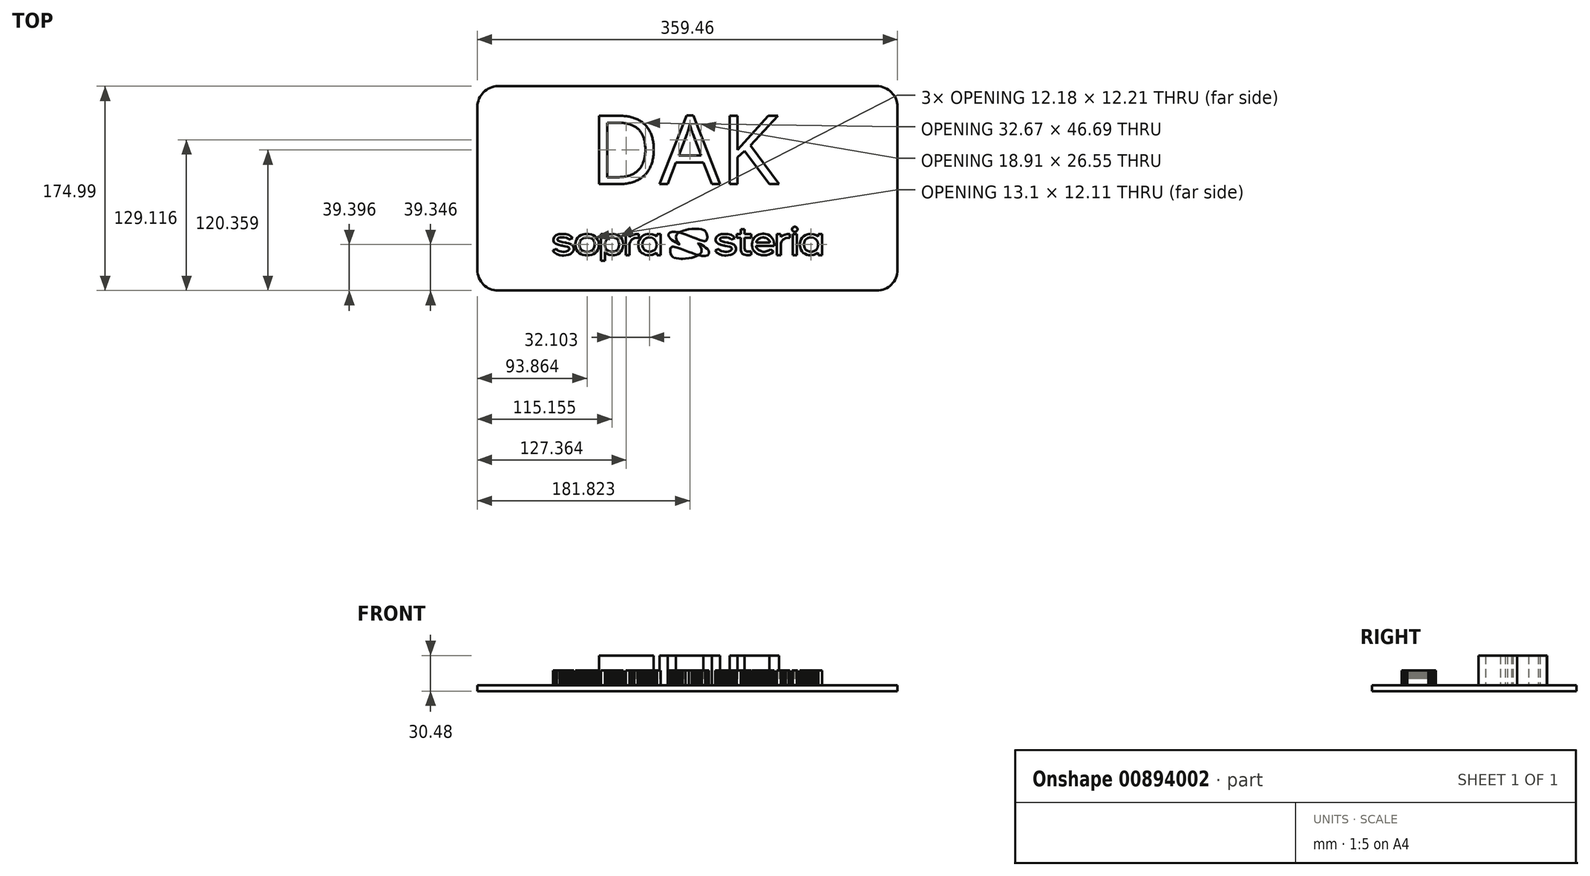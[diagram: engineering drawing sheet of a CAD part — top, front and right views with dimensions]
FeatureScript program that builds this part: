
annotation { "Feature Type Name" : "Feature", "Feature Type Description" : "" }
export const myFeature = defineFeature(function(context is Context, id is Id, definition is map)
    precondition{}
    {
        {
            var Q0;
            Q0=qCreatedBy(makeId("Top.planeOp"),FACE);
            var sketch = newSketch(context, id + "F0", { "sketchPlane" : qUnion([Q0])});
            skLineSegment(sketch, "E0", {"start": v(10.08, -9.2) * mm, "end": v(10.03, -9.23) * mm});
            skLineSegment(sketch, "E1", {"start": v(10.03, -9.23) * mm, "end": v(9.5, -9.56) * mm});
            skLineSegment(sketch, "E2", {"start": v(9.5, -9.56) * mm, "end": v(9.45, -9.6) * mm});
            skLineSegment(sketch, "E3", {"start": v(9.45, -9.6) * mm, "end": v(9.39, -9.63) * mm});
            skLineSegment(sketch, "E4", {"start": v(9.39, -9.63) * mm, "end": v(9.45, -9.64) * mm});
            skLineSegment(sketch, "E5", {"start": v(9.45, -9.64) * mm, "end": v(10.2, -9.84) * mm});
            skLineSegment(sketch, "E6", {"start": v(10.2, -9.84) * mm, "end": v(12.47, -10.24) * mm});
            skLineSegment(sketch, "E7", {"start": v(12.47, -10.24) * mm, "end": v(15.18, -10.28) * mm});
            skLineSegment(sketch, "E8", {"start": v(15.18, -10.28) * mm, "end": v(17.26, -9.63) * mm});
            skLineSegment(sketch, "E9", {"start": v(17.26, -9.63) * mm, "end": v(18.28, -8.57) * mm});
            skLineSegment(sketch, "E10", {"start": v(18.28, -8.57) * mm, "end": v(18.41, -8.16) * mm});
            skLineSegment(sketch, "E11", {"start": v(18.41, -8.16) * mm, "end": v(18.5, -7.87) * mm});
            skLineSegment(sketch, "E12", {"start": v(18.5, -7.87) * mm, "end": v(18.46, -6.9) * mm});
            skLineSegment(sketch, "E13", {"start": v(18.46, -6.9) * mm, "end": v(17.92, -5.66) * mm});
            skLineSegment(sketch, "E14", {"start": v(17.92, -5.66) * mm, "end": v(16.94, -4.44) * mm});
            skLineSegment(sketch, "E15", {"start": v(16.94, -4.44) * mm, "end": v(15.64, -3.27) * mm});
            skLineSegment(sketch, "E16", {"start": v(15.64, -3.27) * mm, "end": v(14.14, -2.18) * mm});
            skLineSegment(sketch, "E17", {"start": v(14.14, -2.18) * mm, "end": v(12.59, -1.19) * mm});
            skLineSegment(sketch, "E18", {"start": v(12.59, -1.19) * mm, "end": v(11.1, -0.32) * mm});
            skLineSegment(sketch, "E19", {"start": v(11.1, -0.32) * mm, "end": v(10.12, 0.22) * mm});
            skLineSegment(sketch, "E20", {"start": v(10.12, 0.22) * mm, "end": v(9.8, 0.4) * mm});
            skLineSegment(sketch, "E21", {"start": v(9.8, 0.4) * mm, "end": v(9.7, 0.45) * mm});
            skLineSegment(sketch, "E22", {"start": v(9.7, 0.45) * mm, "end": v(9.38, 0.56) * mm});
            skLineSegment(sketch, "E23", {"start": v(9.38, 0.56) * mm, "end": v(9.13, 0.54) * mm});
            skLineSegment(sketch, "E24", {"start": v(9.13, 0.54) * mm, "end": v(9.08, 0.36) * mm});
            skLineSegment(sketch, "E25", {"start": v(9.08, 0.36) * mm, "end": v(9.2, 0.12) * mm});
            skLineSegment(sketch, "E26", {"start": v(9.2, 0.12) * mm, "end": v(9.27, 0.05) * mm});
            skLineSegment(sketch, "E27", {"start": v(9.27, 0.05) * mm, "end": v(9.47, -0.18) * mm});
            skLineSegment(sketch, "E28", {"start": v(9.47, -0.18) * mm, "end": v(10.02, -0.89) * mm});
            skLineSegment(sketch, "E29", {"start": v(10.02, -0.89) * mm, "end": v(10.77, -1.98) * mm});
            skLineSegment(sketch, "E30", {"start": v(10.77, -1.98) * mm, "end": v(11.41, -3.18) * mm});
            skLineSegment(sketch, "E31", {"start": v(11.41, -3.18) * mm, "end": v(11.87, -4.45) * mm});
            skLineSegment(sketch, "E32", {"start": v(11.87, -4.45) * mm, "end": v(12.06, -5.73) * mm});
            skLineSegment(sketch, "E33", {"start": v(12.06, -5.73) * mm, "end": v(11.88, -6.98) * mm});
            skLineSegment(sketch, "E34", {"start": v(11.88, -6.98) * mm, "end": v(11.25, -8.15) * mm});
            skLineSegment(sketch, "E35", {"start": v(11.25, -8.15) * mm, "end": v(10.4, -8.99) * mm});
            skLineSegment(sketch, "E36", {"start": v(10.4, -8.99) * mm, "end": v(10.08, -9.2) * mm});
            skLineSegment(sketch, "E37", {"start": v(45.51, 5.32) * mm, "end": v(42.05, 5.32) * mm});
            skLineSegment(sketch, "E38", {"start": v(42.05, 5.32) * mm, "end": v(42.05, 8.22) * mm});
            skLineSegment(sketch, "E39", {"start": v(42.05, 8.22) * mm, "end": v(45.51, 8.22) * mm});
            skLineSegment(sketch, "E40", {"start": v(45.51, 8.22) * mm, "end": v(45.51, 12.52) * mm});
            skLineSegment(sketch, "E41", {"start": v(45.51, 12.52) * mm, "end": v(48.87, 12.52) * mm});
            skLineSegment(sketch, "E42", {"start": v(48.87, 12.52) * mm, "end": v(48.87, 8.22) * mm});
            skLineSegment(sketch, "E43", {"start": v(48.87, 8.22) * mm, "end": v(54.4, 8.22) * mm});
            skLineSegment(sketch, "E44", {"start": v(54.4, 8.22) * mm, "end": v(54.4, 5.32) * mm});
            skLineSegment(sketch, "E45", {"start": v(54.4, 5.32) * mm, "end": v(48.87, 5.32) * mm});
            skLineSegment(sketch, "E46", {"start": v(48.87, 5.32) * mm, "end": v(48.87, -3.42) * mm});
            skLineSegment(sketch, "E47", {"start": v(48.87, -3.42) * mm, "end": v(48.87, -3.78) * mm});
            skLineSegment(sketch, "E48", {"start": v(48.87, -3.78) * mm, "end": v(49, -4.86) * mm});
            skLineSegment(sketch, "E49", {"start": v(49, -4.86) * mm, "end": v(49.52, -5.9) * mm});
            skLineSegment(sketch, "E50", {"start": v(49.52, -5.9) * mm, "end": v(50.56, -6.53) * mm});
            skLineSegment(sketch, "E51", {"start": v(50.56, -6.53) * mm, "end": v(51.85, -6.74) * mm});
            skLineSegment(sketch, "E52", {"start": v(51.85, -6.74) * mm, "end": v(52.28, -6.74) * mm});
            skLineSegment(sketch, "E53", {"start": v(52.28, -6.74) * mm, "end": v(52.48, -6.74) * mm});
            skLineSegment(sketch, "E54", {"start": v(52.48, -6.74) * mm, "end": v(53.08, -6.7) * mm});
            skLineSegment(sketch, "E55", {"start": v(53.08, -6.7) * mm, "end": v(53.81, -6.6) * mm});
            skLineSegment(sketch, "E56", {"start": v(53.81, -6.6) * mm, "end": v(54.34, -6.49) * mm});
            skLineSegment(sketch, "E57", {"start": v(54.34, -6.49) * mm, "end": v(54.55, -6.44) * mm});
            skLineSegment(sketch, "E58", {"start": v(54.55, -6.44) * mm, "end": v(54.55, -9.46) * mm});
            skLineSegment(sketch, "E59", {"start": v(54.55, -9.46) * mm, "end": v(54.26, -9.5) * mm});
            skLineSegment(sketch, "E60", {"start": v(54.26, -9.5) * mm, "end": v(52.94, -9.65) * mm});
            skLineSegment(sketch, "E61", {"start": v(52.94, -9.65) * mm, "end": v(51.64, -9.71) * mm});
            skLineSegment(sketch, "E62", {"start": v(51.64, -9.71) * mm, "end": v(51.21, -9.71) * mm});
            skLineSegment(sketch, "E63", {"start": v(51.21, -9.71) * mm, "end": v(50.77, -9.71) * mm});
            skLineSegment(sketch, "E64", {"start": v(50.77, -9.71) * mm, "end": v(49.45, -9.54) * mm});
            skLineSegment(sketch, "E65", {"start": v(49.45, -9.54) * mm, "end": v(48.09, -9.08) * mm});
            skLineSegment(sketch, "E66", {"start": v(48.09, -9.08) * mm, "end": v(47.08, -8.4) * mm});
            skLineSegment(sketch, "E67", {"start": v(47.08, -8.4) * mm, "end": v(46.38, -7.54) * mm});
            skLineSegment(sketch, "E68", {"start": v(46.38, -7.54) * mm, "end": v(45.92, -6.6) * mm});
            skLineSegment(sketch, "E69", {"start": v(45.92, -6.6) * mm, "end": v(45.66, -5.61) * mm});
            skLineSegment(sketch, "E70", {"start": v(45.66, -5.61) * mm, "end": v(45.54, -4.66) * mm});
            skLineSegment(sketch, "E71", {"start": v(45.54, -4.66) * mm, "end": v(45.51, -4.02) * mm});
            skLineSegment(sketch, "E72", {"start": v(45.51, -4.02) * mm, "end": v(45.51, -3.81) * mm});
            skLineSegment(sketch, "E73", {"start": v(45.51, -3.81) * mm, "end": v(45.51, 5.32) * mm});
            skLineSegment(sketch, "E74", {"start": v(93.55, -9.75) * mm, "end": v(90.11, -9.75) * mm});
            skLineSegment(sketch, "E75", {"start": v(90.11, -9.75) * mm, "end": v(90.11, 8.23) * mm});
            skLineSegment(sketch, "E76", {"start": v(90.11, 8.23) * mm, "end": v(93.55, 8.23) * mm});
            skLineSegment(sketch, "E77", {"start": v(93.55, 8.23) * mm, "end": v(93.55, -9.75) * mm});
            skLineSegment(sketch, "E78", {"start": v(96.13, -0.6) * mm, "end": v(96.13, 0) * mm});
            skLineSegment(sketch, "E79", {"start": v(96.13, 0) * mm, "end": v(96.37, 1.74) * mm});
            skLineSegment(sketch, "E80", {"start": v(96.37, 1.74) * mm, "end": v(97.04, 3.68) * mm});
            skLineSegment(sketch, "E81", {"start": v(97.04, 3.68) * mm, "end": v(98.06, 5.25) * mm});
            skLineSegment(sketch, "E82", {"start": v(98.06, 5.25) * mm, "end": v(99.34, 6.48) * mm});
            skLineSegment(sketch, "E83", {"start": v(99.34, 6.48) * mm, "end": v(100.8, 7.39) * mm});
            skLineSegment(sketch, "E84", {"start": v(100.8, 7.39) * mm, "end": v(102.34, 8) * mm});
            skLineSegment(sketch, "E85", {"start": v(102.34, 8) * mm, "end": v(103.9, 8.36) * mm});
            skLineSegment(sketch, "E86", {"start": v(103.9, 8.36) * mm, "end": v(105.02, 8.47) * mm});
            skLineSegment(sketch, "E87", {"start": v(105.02, 8.47) * mm, "end": v(105.4, 8.47) * mm});
            skLineSegment(sketch, "E88", {"start": v(105.4, 8.47) * mm, "end": v(106.1, 8.47) * mm});
            skLineSegment(sketch, "E89", {"start": v(106.1, 8.47) * mm, "end": v(108.22, 8.08) * mm});
            skLineSegment(sketch, "E90", {"start": v(108.22, 8.08) * mm, "end": v(110.22, 7.23) * mm});
            skLineSegment(sketch, "E91", {"start": v(110.22, 7.23) * mm, "end": v(111.4, 6.38) * mm});
            skLineSegment(sketch, "E92", {"start": v(111.4, 6.38) * mm, "end": v(111.8, 6) * mm});
            skLineSegment(sketch, "E93", {"start": v(111.8, 6) * mm, "end": v(111.98, 8.23) * mm});
            skLineSegment(sketch, "E94", {"start": v(111.98, 8.23) * mm, "end": v(115.12, 8.23) * mm});
            skLineSegment(sketch, "E95", {"start": v(115.12, 8.23) * mm, "end": v(115.12, -9.8) * mm});
            skLineSegment(sketch, "E96", {"start": v(115.12, -9.8) * mm, "end": v(111.98, -9.8) * mm});
            skLineSegment(sketch, "E97", {"start": v(111.98, -9.8) * mm, "end": v(111.8, -7.4) * mm});
            skLineSegment(sketch, "E98", {"start": v(111.8, -7.4) * mm, "end": v(111.4, -7.78) * mm});
            skLineSegment(sketch, "E99", {"start": v(111.4, -7.78) * mm, "end": v(110.19, -8.6) * mm});
            skLineSegment(sketch, "E100", {"start": v(110.19, -8.6) * mm, "end": v(108.17, -9.42) * mm});
            skLineSegment(sketch, "E101", {"start": v(108.17, -9.42) * mm, "end": v(106.06, -9.8) * mm});
            skLineSegment(sketch, "E102", {"start": v(106.06, -9.8) * mm, "end": v(105.36, -9.8) * mm});
            skLineSegment(sketch, "E103", {"start": v(105.36, -9.8) * mm, "end": v(104.95, -9.8) * mm});
            skLineSegment(sketch, "E104", {"start": v(104.95, -9.8) * mm, "end": v(103.72, -9.67) * mm});
            skLineSegment(sketch, "E105", {"start": v(103.72, -9.67) * mm, "end": v(102.1, -9.3) * mm});
            skLineSegment(sketch, "E106", {"start": v(102.1, -9.3) * mm, "end": v(100.54, -8.65) * mm});
            skLineSegment(sketch, "E107", {"start": v(100.54, -8.65) * mm, "end": v(99.13, -7.7) * mm});
            skLineSegment(sketch, "E108", {"start": v(99.13, -7.7) * mm, "end": v(97.91, -6.45) * mm});
            skLineSegment(sketch, "E109", {"start": v(97.91, -6.45) * mm, "end": v(96.96, -4.86) * mm});
            skLineSegment(sketch, "E110", {"start": v(96.96, -4.86) * mm, "end": v(96.35, -2.9) * mm});
            skLineSegment(sketch, "E111", {"start": v(96.35, -2.9) * mm, "end": v(96.13, -1.17) * mm});
            skLineSegment(sketch, "E112", {"start": v(96.13, -1.17) * mm, "end": v(96.13, -0.6) * mm});
            skLineSegment(sketch, "E113", {"start": v(99.62, -0.63) * mm, "end": v(99.62, -1.04) * mm});
            skLineSegment(sketch, "E114", {"start": v(99.62, -1.04) * mm, "end": v(99.8, -2.3) * mm});
            skLineSegment(sketch, "E115", {"start": v(99.8, -2.3) * mm, "end": v(100.28, -3.65) * mm});
            skLineSegment(sketch, "E116", {"start": v(100.28, -3.65) * mm, "end": v(101, -4.72) * mm});
            skLineSegment(sketch, "E117", {"start": v(101, -4.72) * mm, "end": v(101.88, -5.53) * mm});
            skLineSegment(sketch, "E118", {"start": v(101.88, -5.53) * mm, "end": v(102.85, -6.1) * mm});
            skLineSegment(sketch, "E119", {"start": v(102.85, -6.1) * mm, "end": v(103.84, -6.48) * mm});
            skLineSegment(sketch, "E120", {"start": v(103.84, -6.48) * mm, "end": v(104.77, -6.69) * mm});
            skLineSegment(sketch, "E121", {"start": v(104.77, -6.69) * mm, "end": v(105.37, -6.75) * mm});
            skLineSegment(sketch, "E122", {"start": v(105.37, -6.75) * mm, "end": v(105.58, -6.75) * mm});
            skLineSegment(sketch, "E123", {"start": v(105.58, -6.75) * mm, "end": v(106.2, -6.75) * mm});
            skLineSegment(sketch, "E124", {"start": v(106.2, -6.75) * mm, "end": v(108.09, -6.36) * mm});
            skLineSegment(sketch, "E125", {"start": v(108.09, -6.36) * mm, "end": v(110.06, -5.2) * mm});
            skLineSegment(sketch, "E126", {"start": v(110.06, -5.2) * mm, "end": v(111.34, -3.27) * mm});
            skLineSegment(sketch, "E127", {"start": v(111.34, -3.27) * mm, "end": v(111.8, -1.23) * mm});
            skLineSegment(sketch, "E128", {"start": v(111.8, -1.23) * mm, "end": v(111.8, -0.56) * mm});
            skLineSegment(sketch, "E129", {"start": v(111.8, -0.56) * mm, "end": v(111.8, 0.11) * mm});
            skLineSegment(sketch, "E130", {"start": v(111.8, 0.11) * mm, "end": v(111.3, 2.13) * mm});
            skLineSegment(sketch, "E131", {"start": v(111.3, 2.13) * mm, "end": v(109.92, 4) * mm});
            skLineSegment(sketch, "E132", {"start": v(109.92, 4) * mm, "end": v(107.92, 5.1) * mm});
            skLineSegment(sketch, "E133", {"start": v(107.92, 5.1) * mm, "end": v(106.13, 5.46) * mm});
            skLineSegment(sketch, "E134", {"start": v(106.13, 5.46) * mm, "end": v(105.54, 5.46) * mm});
            skLineSegment(sketch, "E135", {"start": v(105.54, 5.46) * mm, "end": v(105.34, 5.46) * mm});
            skLineSegment(sketch, "E136", {"start": v(105.34, 5.46) * mm, "end": v(104.74, 5.4) * mm});
            skLineSegment(sketch, "E137", {"start": v(104.74, 5.4) * mm, "end": v(103.82, 5.21) * mm});
            skLineSegment(sketch, "E138", {"start": v(103.82, 5.21) * mm, "end": v(102.84, 4.85) * mm});
            skLineSegment(sketch, "E139", {"start": v(102.84, 4.85) * mm, "end": v(101.87, 4.28) * mm});
            skLineSegment(sketch, "E140", {"start": v(101.87, 4.28) * mm, "end": v(101, 3.49) * mm});
            skLineSegment(sketch, "E141", {"start": v(101, 3.49) * mm, "end": v(100.28, 2.42) * mm});
            skLineSegment(sketch, "E142", {"start": v(100.28, 2.42) * mm, "end": v(99.8, 1.06) * mm});
            skLineSegment(sketch, "E143", {"start": v(99.8, 1.06) * mm, "end": v(99.62, -0.2) * mm});
            skLineSegment(sketch, "E144", {"start": v(99.62, -0.2) * mm, "end": v(99.62, -0.63) * mm});
            skLineSegment(sketch, "E145", {"start": v(94.08, 12.39) * mm, "end": v(94.08, 12.6) * mm});
            skLineSegment(sketch, "E146", {"start": v(94.08, 12.6) * mm, "end": v(93.9, 13.26) * mm});
            skLineSegment(sketch, "E147", {"start": v(93.9, 13.26) * mm, "end": v(93.42, 13.98) * mm});
            skLineSegment(sketch, "E148", {"start": v(93.42, 13.98) * mm, "end": v(92.7, 14.46) * mm});
            skLineSegment(sketch, "E149", {"start": v(92.7, 14.46) * mm, "end": v(92.05, 14.64) * mm});
            skLineSegment(sketch, "E150", {"start": v(92.05, 14.64) * mm, "end": v(91.83, 14.64) * mm});
            skLineSegment(sketch, "E151", {"start": v(91.83, 14.64) * mm, "end": v(91.61, 14.64) * mm});
            skLineSegment(sketch, "E152", {"start": v(91.61, 14.64) * mm, "end": v(90.96, 14.46) * mm});
            skLineSegment(sketch, "E153", {"start": v(90.96, 14.46) * mm, "end": v(90.24, 13.98) * mm});
            skLineSegment(sketch, "E154", {"start": v(90.24, 13.98) * mm, "end": v(89.76, 13.26) * mm});
            skLineSegment(sketch, "E155", {"start": v(89.76, 13.26) * mm, "end": v(89.58, 12.6) * mm});
            skLineSegment(sketch, "E156", {"start": v(89.58, 12.6) * mm, "end": v(89.58, 12.39) * mm});
            skLineSegment(sketch, "E157", {"start": v(89.58, 12.39) * mm, "end": v(89.58, 12.17) * mm});
            skLineSegment(sketch, "E158", {"start": v(89.58, 12.17) * mm, "end": v(89.76, 11.51) * mm});
            skLineSegment(sketch, "E159", {"start": v(89.76, 11.51) * mm, "end": v(90.24, 10.8) * mm});
            skLineSegment(sketch, "E160", {"start": v(90.24, 10.8) * mm, "end": v(90.96, 10.32) * mm});
            skLineSegment(sketch, "E161", {"start": v(90.96, 10.32) * mm, "end": v(91.61, 10.14) * mm});
            skLineSegment(sketch, "E162", {"start": v(91.61, 10.14) * mm, "end": v(91.83, 10.14) * mm});
            skLineSegment(sketch, "E163", {"start": v(91.83, 10.14) * mm, "end": v(92.05, 10.14) * mm});
            skLineSegment(sketch, "E164", {"start": v(92.05, 10.14) * mm, "end": v(92.7, 10.32) * mm});
            skLineSegment(sketch, "E165", {"start": v(92.7, 10.32) * mm, "end": v(93.42, 10.8) * mm});
            skLineSegment(sketch, "E166", {"start": v(93.42, 10.8) * mm, "end": v(93.9, 11.51) * mm});
            skLineSegment(sketch, "E167", {"start": v(93.9, 11.51) * mm, "end": v(94.08, 12.17) * mm});
            skLineSegment(sketch, "E168", {"start": v(94.08, 12.17) * mm, "end": v(94.08, 12.39) * mm});
            skLineSegment(sketch, "E169", {"start": v(87.6, 5.14) * mm, "end": v(87.6, 8.19) * mm});
            skLineSegment(sketch, "E170", {"start": v(87.6, 8.19) * mm, "end": v(87.01, 8.24) * mm});
            skLineSegment(sketch, "E171", {"start": v(87.01, 8.24) * mm, "end": v(85.24, 8.2) * mm});
            skLineSegment(sketch, "E172", {"start": v(85.24, 8.2) * mm, "end": v(83.2, 7.81) * mm});
            skLineSegment(sketch, "E173", {"start": v(83.2, 7.81) * mm, "end": v(81.46, 6.99) * mm});
            skLineSegment(sketch, "E174", {"start": v(81.46, 6.99) * mm, "end": v(80.3, 6.1) * mm});
            skLineSegment(sketch, "E175", {"start": v(80.3, 6.1) * mm, "end": v(79.96, 5.74) * mm});
            skLineSegment(sketch, "E176", {"start": v(79.96, 5.74) * mm, "end": v(79.79, 8.23) * mm});
            skLineSegment(sketch, "E177", {"start": v(79.79, 8.23) * mm, "end": v(76.52, 8.23) * mm});
            skLineSegment(sketch, "E178", {"start": v(76.52, 8.23) * mm, "end": v(76.52, -9.78) * mm});
            skLineSegment(sketch, "E179", {"start": v(76.52, -9.78) * mm, "end": v(79.96, -9.78) * mm});
            skLineSegment(sketch, "E180", {"start": v(79.96, -9.78) * mm, "end": v(79.96, -0.45) * mm});
            skLineSegment(sketch, "E181", {"start": v(79.96, -0.45) * mm, "end": v(79.96, 0.05) * mm});
            skLineSegment(sketch, "E182", {"start": v(79.96, 0.05) * mm, "end": v(80.38, 1.57) * mm});
            skLineSegment(sketch, "E183", {"start": v(80.38, 1.57) * mm, "end": v(81.7, 3.44) * mm});
            skLineSegment(sketch, "E184", {"start": v(81.7, 3.44) * mm, "end": v(84.07, 4.76) * mm});
            skLineSegment(sketch, "E185", {"start": v(84.07, 4.76) * mm, "end": v(86.72, 5.2) * mm});
            skLineSegment(sketch, "E186", {"start": v(86.72, 5.2) * mm, "end": v(87.6, 5.14) * mm});
            skLineSegment(sketch, "E187", {"start": v(70.47, 0.88) * mm, "end": v(70.47, 1.1) * mm});
            skLineSegment(sketch, "E188", {"start": v(70.47, 1.1) * mm, "end": v(70.35, 1.78) * mm});
            skLineSegment(sketch, "E189", {"start": v(70.35, 1.78) * mm, "end": v(70.03, 2.62) * mm});
            skLineSegment(sketch, "E190", {"start": v(70.03, 2.62) * mm, "end": v(69.53, 3.38) * mm});
            skLineSegment(sketch, "E191", {"start": v(69.53, 3.38) * mm, "end": v(68.86, 4.04) * mm});
            skLineSegment(sketch, "E192", {"start": v(68.86, 4.04) * mm, "end": v(68.04, 4.6) * mm});
            skLineSegment(sketch, "E193", {"start": v(68.04, 4.6) * mm, "end": v(67.11, 5.01) * mm});
            skLineSegment(sketch, "E194", {"start": v(67.11, 5.01) * mm, "end": v(66.08, 5.28) * mm});
            skLineSegment(sketch, "E195", {"start": v(66.08, 5.28) * mm, "end": v(65.26, 5.37) * mm});
            skLineSegment(sketch, "E196", {"start": v(65.26, 5.37) * mm, "end": v(64.98, 5.37) * mm});
            skLineSegment(sketch, "E197", {"start": v(64.98, 5.37) * mm, "end": v(64.4, 5.37) * mm});
            skLineSegment(sketch, "E198", {"start": v(64.4, 5.37) * mm, "end": v(62.69, 5.02) * mm});
            skLineSegment(sketch, "E199", {"start": v(62.69, 5.02) * mm, "end": v(60.78, 4.06) * mm});
            skLineSegment(sketch, "E200", {"start": v(60.78, 4.06) * mm, "end": v(59.44, 2.63) * mm});
            skLineSegment(sketch, "E201", {"start": v(59.44, 2.63) * mm, "end": v(58.89, 1.33) * mm});
            skLineSegment(sketch, "E202", {"start": v(58.89, 1.33) * mm, "end": v(58.85, 0.88) * mm});
            skLineSegment(sketch, "E203", {"start": v(58.85, 0.88) * mm, "end": v(70.47, 0.88) * mm});
            skLineSegment(sketch, "E204", {"start": v(55.22, -0.66) * mm, "end": v(55.22, -0.16) * mm});
            skLineSegment(sketch, "E205", {"start": v(55.22, -0.16) * mm, "end": v(55.4, 1.35) * mm});
            skLineSegment(sketch, "E206", {"start": v(55.4, 1.35) * mm, "end": v(55.95, 3.16) * mm});
            skLineSegment(sketch, "E207", {"start": v(55.95, 3.16) * mm, "end": v(56.83, 4.74) * mm});
            skLineSegment(sketch, "E208", {"start": v(56.83, 4.74) * mm, "end": v(58, 6.07) * mm});
            skLineSegment(sketch, "E209", {"start": v(58, 6.07) * mm, "end": v(59.42, 7.14) * mm});
            skLineSegment(sketch, "E210", {"start": v(59.42, 7.14) * mm, "end": v(61.07, 7.93) * mm});
            skLineSegment(sketch, "E211", {"start": v(61.07, 7.93) * mm, "end": v(62.92, 8.42) * mm});
            skLineSegment(sketch, "E212", {"start": v(62.92, 8.42) * mm, "end": v(64.43, 8.58) * mm});
            skLineSegment(sketch, "E213", {"start": v(64.43, 8.58) * mm, "end": v(64.93, 8.58) * mm});
            skLineSegment(sketch, "E214", {"start": v(64.93, 8.58) * mm, "end": v(65.43, 8.58) * mm});
            skLineSegment(sketch, "E215", {"start": v(65.43, 8.58) * mm, "end": v(66.92, 8.4) * mm});
            skLineSegment(sketch, "E216", {"start": v(66.92, 8.4) * mm, "end": v(68.71, 7.87) * mm});
            skLineSegment(sketch, "E217", {"start": v(68.71, 7.87) * mm, "end": v(70.3, 7.05) * mm});
            skLineSegment(sketch, "E218", {"start": v(70.3, 7.05) * mm, "end": v(71.66, 5.95) * mm});
            skLineSegment(sketch, "E219", {"start": v(71.66, 5.95) * mm, "end": v(72.75, 4.63) * mm});
            skLineSegment(sketch, "E220", {"start": v(72.75, 4.63) * mm, "end": v(73.56, 3.11) * mm});
            skLineSegment(sketch, "E221", {"start": v(73.56, 3.11) * mm, "end": v(74.07, 1.44) * mm});
            skLineSegment(sketch, "E222", {"start": v(74.07, 1.44) * mm, "end": v(74.24, 0.1) * mm});
            skLineSegment(sketch, "E223", {"start": v(74.24, 0.1) * mm, "end": v(74.24, -0.35) * mm});
            skLineSegment(sketch, "E224", {"start": v(74.24, -0.35) * mm, "end": v(74.23, -0.82) * mm});
            skLineSegment(sketch, "E225", {"start": v(74.23, -0.82) * mm, "end": v(74.19, -1.64) * mm});
            skLineSegment(sketch, "E226", {"start": v(74.19, -1.64) * mm, "end": v(74.17, -1.8) * mm});
            skLineSegment(sketch, "E227", {"start": v(74.17, -1.8) * mm, "end": v(58.8, -1.87) * mm});
            skLineSegment(sketch, "E228", {"start": v(58.8, -1.87) * mm, "end": v(58.82, -2.36) * mm});
            skLineSegment(sketch, "E229", {"start": v(58.82, -2.36) * mm, "end": v(59.43, -3.8) * mm});
            skLineSegment(sketch, "E230", {"start": v(59.43, -3.8) * mm, "end": v(60.94, -5.35) * mm});
            skLineSegment(sketch, "E231", {"start": v(60.94, -5.35) * mm, "end": v(63.04, -6.38) * mm});
            skLineSegment(sketch, "E232", {"start": v(63.04, -6.38) * mm, "end": v(64.86, -6.75) * mm});
            skLineSegment(sketch, "E233", {"start": v(64.86, -6.75) * mm, "end": v(65.46, -6.75) * mm});
            skLineSegment(sketch, "E234", {"start": v(65.46, -6.75) * mm, "end": v(66.06, -6.75) * mm});
            skLineSegment(sketch, "E235", {"start": v(66.06, -6.75) * mm, "end": v(67.85, -6.4) * mm});
            skLineSegment(sketch, "E236", {"start": v(67.85, -6.4) * mm, "end": v(69.64, -5.64) * mm});
            skLineSegment(sketch, "E237", {"start": v(69.64, -5.64) * mm, "end": v(70.75, -4.89) * mm});
            skLineSegment(sketch, "E238", {"start": v(70.75, -4.89) * mm, "end": v(71.14, -4.54) * mm});
            skLineSegment(sketch, "E239", {"start": v(71.14, -4.54) * mm, "end": v(73.6, -6.7) * mm});
            skLineSegment(sketch, "E240", {"start": v(73.6, -6.7) * mm, "end": v(73.16, -7.12) * mm});
            skLineSegment(sketch, "E241", {"start": v(73.16, -7.12) * mm, "end": v(71.68, -8.2) * mm});
            skLineSegment(sketch, "E242", {"start": v(71.68, -8.2) * mm, "end": v(69.69, -9.17) * mm});
            skLineSegment(sketch, "E243", {"start": v(69.69, -9.17) * mm, "end": v(67.61, -9.68) * mm});
            skLineSegment(sketch, "E244", {"start": v(67.61, -9.68) * mm, "end": v(66, -9.83) * mm});
            skLineSegment(sketch, "E245", {"start": v(66, -9.83) * mm, "end": v(65.46, -9.83) * mm});
            skLineSegment(sketch, "E246", {"start": v(65.46, -9.83) * mm, "end": v(64.92, -9.83) * mm});
            skLineSegment(sketch, "E247", {"start": v(64.92, -9.83) * mm, "end": v(63.28, -9.67) * mm});
            skLineSegment(sketch, "E248", {"start": v(63.28, -9.67) * mm, "end": v(61.3, -9.2) * mm});
            skLineSegment(sketch, "E249", {"start": v(61.3, -9.2) * mm, "end": v(59.56, -8.42) * mm});
            skLineSegment(sketch, "E250", {"start": v(59.56, -8.42) * mm, "end": v(58.07, -7.37) * mm});
            skLineSegment(sketch, "E251", {"start": v(58.07, -7.37) * mm, "end": v(56.86, -6.07) * mm});
            skLineSegment(sketch, "E252", {"start": v(56.86, -6.07) * mm, "end": v(55.97, -4.52) * mm});
            skLineSegment(sketch, "E253", {"start": v(55.97, -4.52) * mm, "end": v(55.4, -2.76) * mm});
            skLineSegment(sketch, "E254", {"start": v(55.4, -2.76) * mm, "end": v(55.22, -1.3) * mm});
            skLineSegment(sketch, "E255", {"start": v(55.22, -1.3) * mm, "end": v(55.22, -0.8) * mm});
            skLineSegment(sketch, "E256", {"start": v(55.22, -0.8) * mm, "end": v(55.22, -0.66) * mm});
            skLineSegment(sketch, "E257", {"start": v(34.69, 0.96) * mm, "end": v(34.05, 1.07) * mm});
            skLineSegment(sketch, "E258", {"start": v(34.05, 1.07) * mm, "end": v(32.15, 1.41) * mm});
            skLineSegment(sketch, "E259", {"start": v(32.15, 1.41) * mm, "end": v(29.96, 1.92) * mm});
            skLineSegment(sketch, "E260", {"start": v(29.96, 1.92) * mm, "end": v(28.4, 2.61) * mm});
            skLineSegment(sketch, "E261", {"start": v(28.4, 2.61) * mm, "end": v(27.82, 3.37) * mm});
            skLineSegment(sketch, "E262", {"start": v(27.82, 3.37) * mm, "end": v(27.82, 3.62) * mm});
            skLineSegment(sketch, "E263", {"start": v(27.82, 3.62) * mm, "end": v(27.82, 3.81) * mm});
            skLineSegment(sketch, "E264", {"start": v(27.82, 3.81) * mm, "end": v(28.03, 4.38) * mm});
            skLineSegment(sketch, "E265", {"start": v(28.03, 4.38) * mm, "end": v(28.72, 5) * mm});
            skLineSegment(sketch, "E266", {"start": v(28.72, 5) * mm, "end": v(29.98, 5.44) * mm});
            skLineSegment(sketch, "E267", {"start": v(29.98, 5.44) * mm, "end": v(31.42, 5.6) * mm});
            skLineSegment(sketch, "E268", {"start": v(31.42, 5.6) * mm, "end": v(31.9, 5.6) * mm});
            skLineSegment(sketch, "E269", {"start": v(31.9, 5.6) * mm, "end": v(32.32, 5.6) * mm});
            skLineSegment(sketch, "E270", {"start": v(32.32, 5.6) * mm, "end": v(33.61, 5.5) * mm});
            skLineSegment(sketch, "E271", {"start": v(33.61, 5.5) * mm, "end": v(35.25, 5.14) * mm});
            skLineSegment(sketch, "E272", {"start": v(35.25, 5.14) * mm, "end": v(36.6, 4.49) * mm});
            skLineSegment(sketch, "E273", {"start": v(36.6, 4.49) * mm, "end": v(37.32, 3.77) * mm});
            skLineSegment(sketch, "E274", {"start": v(37.32, 3.77) * mm, "end": v(37.45, 3.48) * mm});
            skLineSegment(sketch, "E275", {"start": v(37.45, 3.48) * mm, "end": v(40.64, 4.83) * mm});
            skLineSegment(sketch, "E276", {"start": v(40.64, 4.83) * mm, "end": v(40.41, 5.28) * mm});
            skLineSegment(sketch, "E277", {"start": v(40.41, 5.28) * mm, "end": v(39.3, 6.43) * mm});
            skLineSegment(sketch, "E278", {"start": v(39.3, 6.43) * mm, "end": v(37.25, 7.56) * mm});
            skLineSegment(sketch, "E279", {"start": v(37.25, 7.56) * mm, "end": v(34.64, 8.24) * mm});
            skLineSegment(sketch, "E280", {"start": v(34.64, 8.24) * mm, "end": v(32.4, 8.46) * mm});
            skLineSegment(sketch, "E281", {"start": v(32.4, 8.46) * mm, "end": v(31.66, 8.46) * mm});
            skLineSegment(sketch, "E282", {"start": v(31.66, 8.46) * mm, "end": v(30.98, 8.46) * mm});
            skLineSegment(sketch, "E283", {"start": v(30.98, 8.46) * mm, "end": v(28.95, 8.19) * mm});
            skLineSegment(sketch, "E284", {"start": v(28.95, 8.19) * mm, "end": v(26.53, 7.31) * mm});
            skLineSegment(sketch, "E285", {"start": v(26.53, 7.31) * mm, "end": v(24.8, 5.75) * mm});
            skLineSegment(sketch, "E286", {"start": v(24.8, 5.75) * mm, "end": v(24.13, 4) * mm});
            skLineSegment(sketch, "E287", {"start": v(24.13, 4) * mm, "end": v(24.13, 3.41) * mm});
            skLineSegment(sketch, "E288", {"start": v(24.13, 3.41) * mm, "end": v(24.13, 2.9) * mm});
            skLineSegment(sketch, "E289", {"start": v(24.13, 2.9) * mm, "end": v(24.66, 1.4) * mm});
            skLineSegment(sketch, "E290", {"start": v(24.66, 1.4) * mm, "end": v(26.18, 0.02) * mm});
            skLineSegment(sketch, "E291", {"start": v(26.18, 0.02) * mm, "end": v(28.59, -0.93) * mm});
            skLineSegment(sketch, "E292", {"start": v(28.59, -0.93) * mm, "end": v(31, -1.5) * mm});
            skLineSegment(sketch, "E293", {"start": v(31, -1.5) * mm, "end": v(31.8, -1.66) * mm});
            skLineSegment(sketch, "E294", {"start": v(31.8, -1.66) * mm, "end": v(32.38, -1.77) * mm});
            skLineSegment(sketch, "E295", {"start": v(32.38, -1.77) * mm, "end": v(34.1, -2.08) * mm});
            skLineSegment(sketch, "E296", {"start": v(34.1, -2.08) * mm, "end": v(36.07, -2.55) * mm});
            skLineSegment(sketch, "E297", {"start": v(36.07, -2.55) * mm, "end": v(37.43, -3.23) * mm});
            skLineSegment(sketch, "E298", {"start": v(37.43, -3.23) * mm, "end": v(37.94, -4.02) * mm});
            skLineSegment(sketch, "E299", {"start": v(37.94, -4.02) * mm, "end": v(37.94, -4.28) * mm});
            skLineSegment(sketch, "E300", {"start": v(37.94, -4.28) * mm, "end": v(37.94, -4.5) * mm});
            skLineSegment(sketch, "E301", {"start": v(37.94, -4.5) * mm, "end": v(37.65, -5.13) * mm});
            skLineSegment(sketch, "E302", {"start": v(37.65, -5.13) * mm, "end": v(36.76, -5.93) * mm});
            skLineSegment(sketch, "E303", {"start": v(36.76, -5.93) * mm, "end": v(35.19, -6.52) * mm});
            skLineSegment(sketch, "E304", {"start": v(35.19, -6.52) * mm, "end": v(33.45, -6.76) * mm});
            skLineSegment(sketch, "E305", {"start": v(33.45, -6.76) * mm, "end": v(32.87, -6.76) * mm});
            skLineSegment(sketch, "E306", {"start": v(32.87, -6.76) * mm, "end": v(32.4, -6.76) * mm});
            skLineSegment(sketch, "E307", {"start": v(32.4, -6.76) * mm, "end": v(30.97, -6.65) * mm});
            skLineSegment(sketch, "E308", {"start": v(30.97, -6.65) * mm, "end": v(29.22, -6.26) * mm});
            skLineSegment(sketch, "E309", {"start": v(29.22, -6.26) * mm, "end": v(27.82, -5.53) * mm});
            skLineSegment(sketch, "E310", {"start": v(27.82, -5.53) * mm, "end": v(27.05, -4.71) * mm});
            skLineSegment(sketch, "E311", {"start": v(27.05, -4.71) * mm, "end": v(26.91, -4.39) * mm});
            skLineSegment(sketch, "E312", {"start": v(26.91, -4.39) * mm, "end": v(23.82, -5.69) * mm});
            skLineSegment(sketch, "E313", {"start": v(23.82, -5.69) * mm, "end": v(24.05, -6.2) * mm});
            skLineSegment(sketch, "E314", {"start": v(24.05, -6.2) * mm, "end": v(25.14, -7.55) * mm});
            skLineSegment(sketch, "E315", {"start": v(25.14, -7.55) * mm, "end": v(27.1, -8.9) * mm});
            skLineSegment(sketch, "E316", {"start": v(27.1, -8.9) * mm, "end": v(29.55, -9.7) * mm});
            skLineSegment(sketch, "E317", {"start": v(29.55, -9.7) * mm, "end": v(31.65, -9.98) * mm});
            skLineSegment(sketch, "E318", {"start": v(31.65, -9.98) * mm, "end": v(32.36, -9.98) * mm});
            skLineSegment(sketch, "E319", {"start": v(32.36, -9.98) * mm, "end": v(33.01, -9.98) * mm});
            skLineSegment(sketch, "E320", {"start": v(33.01, -9.98) * mm, "end": v(35, -9.81) * mm});
            skLineSegment(sketch, "E321", {"start": v(35, -9.81) * mm, "end": v(37.1, -9.36) * mm});
            skLineSegment(sketch, "E322", {"start": v(37.1, -9.36) * mm, "end": v(38.72, -8.7) * mm});
            skLineSegment(sketch, "E323", {"start": v(38.72, -8.7) * mm, "end": v(39.92, -7.86) * mm});
            skLineSegment(sketch, "E324", {"start": v(39.92, -7.86) * mm, "end": v(40.76, -6.93) * mm});
            skLineSegment(sketch, "E325", {"start": v(40.76, -6.93) * mm, "end": v(41.3, -5.96) * mm});
            skLineSegment(sketch, "E326", {"start": v(41.3, -5.96) * mm, "end": v(41.57, -5.02) * mm});
            skLineSegment(sketch, "E327", {"start": v(41.57, -5.02) * mm, "end": v(41.65, -4.38) * mm});
            skLineSegment(sketch, "E328", {"start": v(41.65, -4.38) * mm, "end": v(41.65, -4.17) * mm});
            skLineSegment(sketch, "E329", {"start": v(41.65, -4.17) * mm, "end": v(41.65, -3.62) * mm});
            skLineSegment(sketch, "E330", {"start": v(41.65, -3.62) * mm, "end": v(41.05, -1.98) * mm});
            skLineSegment(sketch, "E331", {"start": v(41.05, -1.98) * mm, "end": v(39.47, -0.52) * mm});
            skLineSegment(sketch, "E332", {"start": v(39.47, -0.52) * mm, "end": v(37.24, 0.39) * mm});
            skLineSegment(sketch, "E333", {"start": v(37.24, 0.39) * mm, "end": v(35.33, 0.85) * mm});
            skLineSegment(sketch, "E334", {"start": v(35.33, 0.85) * mm, "end": v(34.69, 0.96) * mm});
            skLineSegment(sketch, "E335", {"start": v(-64.22, -9.8) * mm, "end": v(-64.93, -9.8) * mm});
            skLineSegment(sketch, "E336", {"start": v(-64.93, -9.8) * mm, "end": v(-67.05, -9.37) * mm});
            skLineSegment(sketch, "E337", {"start": v(-67.05, -9.37) * mm, "end": v(-69.06, -8.42) * mm});
            skLineSegment(sketch, "E338", {"start": v(-69.06, -8.42) * mm, "end": v(-70.26, -7.48) * mm});
            skLineSegment(sketch, "E339", {"start": v(-70.26, -7.48) * mm, "end": v(-70.66, -7.06) * mm});
            skLineSegment(sketch, "E340", {"start": v(-70.66, -7.06) * mm, "end": v(-70.66, -14.64) * mm});
            skLineSegment(sketch, "E341", {"start": v(-70.66, -14.64) * mm, "end": v(-73.98, -14.64) * mm});
            skLineSegment(sketch, "E342", {"start": v(-73.98, -14.64) * mm, "end": v(-73.98, 8.23) * mm});
            skLineSegment(sketch, "E343", {"start": v(-73.98, 8.23) * mm, "end": v(-70.84, 8.23) * mm});
            skLineSegment(sketch, "E344", {"start": v(-70.84, 8.23) * mm, "end": v(-70.66, 6) * mm});
            skLineSegment(sketch, "E345", {"start": v(-70.66, 6) * mm, "end": v(-70.27, 6.38) * mm});
            skLineSegment(sketch, "E346", {"start": v(-70.27, 6.38) * mm, "end": v(-69.08, 7.23) * mm});
            skLineSegment(sketch, "E347", {"start": v(-69.08, 7.23) * mm, "end": v(-67.08, 8.08) * mm});
            skLineSegment(sketch, "E348", {"start": v(-67.08, 8.08) * mm, "end": v(-64.96, 8.47) * mm});
            skLineSegment(sketch, "E349", {"start": v(-64.96, 8.47) * mm, "end": v(-64.26, 8.47) * mm});
            skLineSegment(sketch, "E350", {"start": v(-64.26, 8.47) * mm, "end": v(-63.89, 8.47) * mm});
            skLineSegment(sketch, "E351", {"start": v(-63.89, 8.47) * mm, "end": v(-62.77, 8.37) * mm});
            skLineSegment(sketch, "E352", {"start": v(-62.77, 8.37) * mm, "end": v(-61.2, 8.06) * mm});
            skLineSegment(sketch, "E353", {"start": v(-61.2, 8.06) * mm, "end": v(-59.66, 7.48) * mm});
            skLineSegment(sketch, "E354", {"start": v(-59.66, 7.48) * mm, "end": v(-58.2, 6.61) * mm});
            skLineSegment(sketch, "E355", {"start": v(-58.2, 6.61) * mm, "end": v(-56.92, 5.4) * mm});
            skLineSegment(sketch, "E356", {"start": v(-56.92, 5.4) * mm, "end": v(-55.9, 3.83) * mm});
            skLineSegment(sketch, "E357", {"start": v(-55.9, 3.83) * mm, "end": v(-55.23, 1.84) * mm});
            skLineSegment(sketch, "E358", {"start": v(-55.23, 1.84) * mm, "end": v(-55, 0.02) * mm});
            skLineSegment(sketch, "E359", {"start": v(-55, 0.02) * mm, "end": v(-55, -0.6) * mm});
            skLineSegment(sketch, "E360", {"start": v(-55, -0.6) * mm, "end": v(-55, -1.2) * mm});
            skLineSegment(sketch, "E361", {"start": v(-55, -1.2) * mm, "end": v(-55.21, -3.03) * mm});
            skLineSegment(sketch, "E362", {"start": v(-55.21, -3.03) * mm, "end": v(-55.83, -5.03) * mm});
            skLineSegment(sketch, "E363", {"start": v(-55.83, -5.03) * mm, "end": v(-56.78, -6.63) * mm});
            skLineSegment(sketch, "E364", {"start": v(-56.78, -6.63) * mm, "end": v(-58, -7.87) * mm});
            skLineSegment(sketch, "E365", {"start": v(-58, -7.87) * mm, "end": v(-59.4, -8.76) * mm});
            skLineSegment(sketch, "E366", {"start": v(-59.4, -8.76) * mm, "end": v(-60.96, -9.36) * mm});
            skLineSegment(sketch, "E367", {"start": v(-60.96, -9.36) * mm, "end": v(-62.59, -9.7) * mm});
            skLineSegment(sketch, "E368", {"start": v(-62.59, -9.7) * mm, "end": v(-63.81, -9.8) * mm});
            skLineSegment(sketch, "E369", {"start": v(-63.81, -9.8) * mm, "end": v(-64.22, -9.8) * mm});
            skLineSegment(sketch, "E370", {"start": v(-64.4, 5.46) * mm, "end": v(-65, 5.46) * mm});
            skLineSegment(sketch, "E371", {"start": v(-65, 5.46) * mm, "end": v(-66.79, 5.1) * mm});
            skLineSegment(sketch, "E372", {"start": v(-66.79, 5.1) * mm, "end": v(-68.78, 4) * mm});
            skLineSegment(sketch, "E373", {"start": v(-68.78, 4) * mm, "end": v(-70.16, 2.13) * mm});
            skLineSegment(sketch, "E374", {"start": v(-70.16, 2.13) * mm, "end": v(-70.66, 0.11) * mm});
            skLineSegment(sketch, "E375", {"start": v(-70.66, 0.11) * mm, "end": v(-70.66, -0.56) * mm});
            skLineSegment(sketch, "E376", {"start": v(-70.66, -0.56) * mm, "end": v(-70.66, -1.23) * mm});
            skLineSegment(sketch, "E377", {"start": v(-70.66, -1.23) * mm, "end": v(-70.2, -3.27) * mm});
            skLineSegment(sketch, "E378", {"start": v(-70.2, -3.27) * mm, "end": v(-68.92, -5.2) * mm});
            skLineSegment(sketch, "E379", {"start": v(-68.92, -5.2) * mm, "end": v(-66.95, -6.36) * mm});
            skLineSegment(sketch, "E380", {"start": v(-66.95, -6.36) * mm, "end": v(-65.07, -6.75) * mm});
            skLineSegment(sketch, "E381", {"start": v(-65.07, -6.75) * mm, "end": v(-64.44, -6.75) * mm});
            skLineSegment(sketch, "E382", {"start": v(-64.44, -6.75) * mm, "end": v(-64.24, -6.75) * mm});
            skLineSegment(sketch, "E383", {"start": v(-64.24, -6.75) * mm, "end": v(-63.63, -6.7) * mm});
            skLineSegment(sketch, "E384", {"start": v(-63.63, -6.7) * mm, "end": v(-62.7, -6.54) * mm});
            skLineSegment(sketch, "E385", {"start": v(-62.7, -6.54) * mm, "end": v(-61.71, -6.22) * mm});
            skLineSegment(sketch, "E386", {"start": v(-61.71, -6.22) * mm, "end": v(-60.74, -5.7) * mm});
            skLineSegment(sketch, "E387", {"start": v(-60.74, -5.7) * mm, "end": v(-59.87, -4.91) * mm});
            skLineSegment(sketch, "E388", {"start": v(-59.87, -4.91) * mm, "end": v(-59.15, -3.84) * mm});
            skLineSegment(sketch, "E389", {"start": v(-59.15, -3.84) * mm, "end": v(-58.66, -2.42) * mm});
            skLineSegment(sketch, "E390", {"start": v(-58.66, -2.42) * mm, "end": v(-58.49, -1.08) * mm});
            skLineSegment(sketch, "E391", {"start": v(-58.49, -1.08) * mm, "end": v(-58.49, -0.63) * mm});
            skLineSegment(sketch, "E392", {"start": v(-58.49, -0.63) * mm, "end": v(-58.49, -0.18) * mm});
            skLineSegment(sketch, "E393", {"start": v(-58.49, -0.18) * mm, "end": v(-58.66, 1.17) * mm});
            skLineSegment(sketch, "E394", {"start": v(-58.66, 1.17) * mm, "end": v(-59.14, 2.58) * mm});
            skLineSegment(sketch, "E395", {"start": v(-59.14, 2.58) * mm, "end": v(-59.86, 3.65) * mm});
            skLineSegment(sketch, "E396", {"start": v(-59.86, 3.65) * mm, "end": v(-60.73, 4.42) * mm});
            skLineSegment(sketch, "E397", {"start": v(-60.73, 4.42) * mm, "end": v(-61.7, 4.95) * mm});
            skLineSegment(sketch, "E398", {"start": v(-61.7, 4.95) * mm, "end": v(-62.68, 5.26) * mm});
            skLineSegment(sketch, "E399", {"start": v(-62.68, 5.26) * mm, "end": v(-63.6, 5.42) * mm});
            skLineSegment(sketch, "E400", {"start": v(-63.6, 5.42) * mm, "end": v(-64.2, 5.46) * mm});
            skLineSegment(sketch, "E401", {"start": v(-64.2, 5.46) * mm, "end": v(-64.4, 5.46) * mm});
            skLineSegment(sketch, "E402", {"start": v(-42.06, -0.6) * mm, "end": v(-42.06, 0) * mm});
            skLineSegment(sketch, "E403", {"start": v(-42.06, 0) * mm, "end": v(-41.81, 1.74) * mm});
            skLineSegment(sketch, "E404", {"start": v(-41.81, 1.74) * mm, "end": v(-41.14, 3.68) * mm});
            skLineSegment(sketch, "E405", {"start": v(-41.14, 3.68) * mm, "end": v(-40.13, 5.25) * mm});
            skLineSegment(sketch, "E406", {"start": v(-40.13, 5.25) * mm, "end": v(-38.85, 6.48) * mm});
            skLineSegment(sketch, "E407", {"start": v(-38.85, 6.48) * mm, "end": v(-37.4, 7.39) * mm});
            skLineSegment(sketch, "E408", {"start": v(-37.4, 7.39) * mm, "end": v(-35.84, 8) * mm});
            skLineSegment(sketch, "E409", {"start": v(-35.84, 8) * mm, "end": v(-34.28, 8.36) * mm});
            skLineSegment(sketch, "E410", {"start": v(-34.28, 8.36) * mm, "end": v(-33.16, 8.47) * mm});
            skLineSegment(sketch, "E411", {"start": v(-33.16, 8.47) * mm, "end": v(-32.79, 8.47) * mm});
            skLineSegment(sketch, "E412", {"start": v(-32.79, 8.47) * mm, "end": v(-32.08, 8.47) * mm});
            skLineSegment(sketch, "E413", {"start": v(-32.08, 8.47) * mm, "end": v(-29.97, 8.08) * mm});
            skLineSegment(sketch, "E414", {"start": v(-29.97, 8.08) * mm, "end": v(-27.97, 7.23) * mm});
            skLineSegment(sketch, "E415", {"start": v(-27.97, 7.23) * mm, "end": v(-26.78, 6.38) * mm});
            skLineSegment(sketch, "E416", {"start": v(-26.78, 6.38) * mm, "end": v(-26.38, 6) * mm});
            skLineSegment(sketch, "E417", {"start": v(-26.38, 6) * mm, "end": v(-26.2, 8.23) * mm});
            skLineSegment(sketch, "E418", {"start": v(-26.2, 8.23) * mm, "end": v(-23.06, 8.23) * mm});
            skLineSegment(sketch, "E419", {"start": v(-23.06, 8.23) * mm, "end": v(-23.06, -9.8) * mm});
            skLineSegment(sketch, "E420", {"start": v(-23.06, -9.8) * mm, "end": v(-26.2, -9.8) * mm});
            skLineSegment(sketch, "E421", {"start": v(-26.2, -9.8) * mm, "end": v(-26.38, -7.4) * mm});
            skLineSegment(sketch, "E422", {"start": v(-26.38, -7.4) * mm, "end": v(-26.79, -7.78) * mm});
            skLineSegment(sketch, "E423", {"start": v(-26.79, -7.78) * mm, "end": v(-28, -8.6) * mm});
            skLineSegment(sketch, "E424", {"start": v(-28, -8.6) * mm, "end": v(-30, -9.42) * mm});
            skLineSegment(sketch, "E425", {"start": v(-30, -9.42) * mm, "end": v(-32.12, -9.8) * mm});
            skLineSegment(sketch, "E426", {"start": v(-32.12, -9.8) * mm, "end": v(-32.83, -9.8) * mm});
            skLineSegment(sketch, "E427", {"start": v(-32.83, -9.8) * mm, "end": v(-33.24, -9.8) * mm});
            skLineSegment(sketch, "E428", {"start": v(-33.24, -9.8) * mm, "end": v(-34.46, -9.67) * mm});
            skLineSegment(sketch, "E429", {"start": v(-34.46, -9.67) * mm, "end": v(-36.09, -9.3) * mm});
            skLineSegment(sketch, "E430", {"start": v(-36.09, -9.3) * mm, "end": v(-37.64, -8.65) * mm});
            skLineSegment(sketch, "E431", {"start": v(-37.64, -8.65) * mm, "end": v(-39.06, -7.7) * mm});
            skLineSegment(sketch, "E432", {"start": v(-39.06, -7.7) * mm, "end": v(-40.27, -6.45) * mm});
            skLineSegment(sketch, "E433", {"start": v(-40.27, -6.45) * mm, "end": v(-41.22, -4.86) * mm});
            skLineSegment(sketch, "E434", {"start": v(-41.22, -4.86) * mm, "end": v(-41.84, -2.9) * mm});
            skLineSegment(sketch, "E435", {"start": v(-41.84, -2.9) * mm, "end": v(-42.06, -1.17) * mm});
            skLineSegment(sketch, "E436", {"start": v(-42.06, -1.17) * mm, "end": v(-42.06, -0.6) * mm});
            skLineSegment(sketch, "E437", {"start": v(-38.56, -0.63) * mm, "end": v(-38.56, -1.04) * mm});
            skLineSegment(sketch, "E438", {"start": v(-38.56, -1.04) * mm, "end": v(-38.38, -2.3) * mm});
            skLineSegment(sketch, "E439", {"start": v(-38.38, -2.3) * mm, "end": v(-37.9, -3.65) * mm});
            skLineSegment(sketch, "E440", {"start": v(-37.9, -3.65) * mm, "end": v(-37.18, -4.72) * mm});
            skLineSegment(sketch, "E441", {"start": v(-37.18, -4.72) * mm, "end": v(-36.3, -5.53) * mm});
            skLineSegment(sketch, "E442", {"start": v(-36.3, -5.53) * mm, "end": v(-35.33, -6.1) * mm});
            skLineSegment(sketch, "E443", {"start": v(-35.33, -6.1) * mm, "end": v(-34.35, -6.48) * mm});
            skLineSegment(sketch, "E444", {"start": v(-34.35, -6.48) * mm, "end": v(-33.42, -6.69) * mm});
            skLineSegment(sketch, "E445", {"start": v(-33.42, -6.69) * mm, "end": v(-32.81, -6.75) * mm});
            skLineSegment(sketch, "E446", {"start": v(-32.81, -6.75) * mm, "end": v(-32.6, -6.75) * mm});
            skLineSegment(sketch, "E447", {"start": v(-32.6, -6.75) * mm, "end": v(-31.98, -6.75) * mm});
            skLineSegment(sketch, "E448", {"start": v(-31.98, -6.75) * mm, "end": v(-30.1, -6.36) * mm});
            skLineSegment(sketch, "E449", {"start": v(-30.1, -6.36) * mm, "end": v(-28.13, -5.2) * mm});
            skLineSegment(sketch, "E450", {"start": v(-28.13, -5.2) * mm, "end": v(-26.84, -3.27) * mm});
            skLineSegment(sketch, "E451", {"start": v(-26.84, -3.27) * mm, "end": v(-26.38, -1.23) * mm});
            skLineSegment(sketch, "E452", {"start": v(-26.38, -1.23) * mm, "end": v(-26.38, -0.56) * mm});
            skLineSegment(sketch, "E453", {"start": v(-26.38, -0.56) * mm, "end": v(-26.38, 0.11) * mm});
            skLineSegment(sketch, "E454", {"start": v(-26.38, 0.11) * mm, "end": v(-26.9, 2.13) * mm});
            skLineSegment(sketch, "E455", {"start": v(-26.9, 2.13) * mm, "end": v(-28.26, 4) * mm});
            skLineSegment(sketch, "E456", {"start": v(-28.26, 4) * mm, "end": v(-30.26, 5.1) * mm});
            skLineSegment(sketch, "E457", {"start": v(-30.26, 5.1) * mm, "end": v(-32.05, 5.46) * mm});
            skLineSegment(sketch, "E458", {"start": v(-32.05, 5.46) * mm, "end": v(-32.64, 5.46) * mm});
            skLineSegment(sketch, "E459", {"start": v(-32.64, 5.46) * mm, "end": v(-32.84, 5.46) * mm});
            skLineSegment(sketch, "E460", {"start": v(-32.84, 5.46) * mm, "end": v(-33.44, 5.4) * mm});
            skLineSegment(sketch, "E461", {"start": v(-33.44, 5.4) * mm, "end": v(-34.37, 5.21) * mm});
            skLineSegment(sketch, "E462", {"start": v(-34.37, 5.21) * mm, "end": v(-35.35, 4.85) * mm});
            skLineSegment(sketch, "E463", {"start": v(-35.35, 4.85) * mm, "end": v(-36.31, 4.28) * mm});
            skLineSegment(sketch, "E464", {"start": v(-36.31, 4.28) * mm, "end": v(-37.19, 3.49) * mm});
            skLineSegment(sketch, "E465", {"start": v(-37.19, 3.49) * mm, "end": v(-37.9, 2.42) * mm});
            skLineSegment(sketch, "E466", {"start": v(-37.9, 2.42) * mm, "end": v(-38.38, 1.06) * mm});
            skLineSegment(sketch, "E467", {"start": v(-38.38, 1.06) * mm, "end": v(-38.56, -0.2) * mm});
            skLineSegment(sketch, "E468", {"start": v(-38.56, -0.2) * mm, "end": v(-38.56, -0.63) * mm});
            skLineSegment(sketch, "E469", {"start": v(-41.8, 5.14) * mm, "end": v(-41.8, 8.19) * mm});
            skLineSegment(sketch, "E470", {"start": v(-41.8, 8.19) * mm, "end": v(-42.4, 8.24) * mm});
            skLineSegment(sketch, "E471", {"start": v(-42.4, 8.24) * mm, "end": v(-44.17, 8.2) * mm});
            skLineSegment(sketch, "E472", {"start": v(-44.17, 8.2) * mm, "end": v(-46.2, 7.81) * mm});
            skLineSegment(sketch, "E473", {"start": v(-46.2, 7.81) * mm, "end": v(-47.94, 6.99) * mm});
            skLineSegment(sketch, "E474", {"start": v(-47.94, 6.99) * mm, "end": v(-49.1, 6.1) * mm});
            skLineSegment(sketch, "E475", {"start": v(-49.1, 6.1) * mm, "end": v(-49.44, 5.74) * mm});
            skLineSegment(sketch, "E476", {"start": v(-49.44, 5.74) * mm, "end": v(-49.62, 8.23) * mm});
            skLineSegment(sketch, "E477", {"start": v(-49.62, 8.23) * mm, "end": v(-52.88, 8.23) * mm});
            skLineSegment(sketch, "E478", {"start": v(-52.88, 8.23) * mm, "end": v(-52.88, -9.78) * mm});
            skLineSegment(sketch, "E479", {"start": v(-52.88, -9.78) * mm, "end": v(-49.44, -9.78) * mm});
            skLineSegment(sketch, "E480", {"start": v(-49.44, -9.78) * mm, "end": v(-49.44, -0.45) * mm});
            skLineSegment(sketch, "E481", {"start": v(-49.44, -0.45) * mm, "end": v(-49.44, 0.05) * mm});
            skLineSegment(sketch, "E482", {"start": v(-49.44, 0.05) * mm, "end": v(-49.03, 1.57) * mm});
            skLineSegment(sketch, "E483", {"start": v(-49.03, 1.57) * mm, "end": v(-47.7, 3.44) * mm});
            skLineSegment(sketch, "E484", {"start": v(-47.7, 3.44) * mm, "end": v(-45.34, 4.76) * mm});
            skLineSegment(sketch, "E485", {"start": v(-45.34, 4.76) * mm, "end": v(-42.68, 5.2) * mm});
            skLineSegment(sketch, "E486", {"start": v(-42.68, 5.2) * mm, "end": v(-41.8, 5.14) * mm});
            skLineSegment(sketch, "E487", {"start": v(-104.25, 0.96) * mm, "end": v(-104.89, 1.07) * mm});
            skLineSegment(sketch, "E488", {"start": v(-104.89, 1.07) * mm, "end": v(-106.79, 1.41) * mm});
            skLineSegment(sketch, "E489", {"start": v(-106.79, 1.41) * mm, "end": v(-108.98, 1.92) * mm});
            skLineSegment(sketch, "E490", {"start": v(-108.98, 1.92) * mm, "end": v(-110.53, 2.61) * mm});
            skLineSegment(sketch, "E491", {"start": v(-110.53, 2.61) * mm, "end": v(-111.12, 3.37) * mm});
            skLineSegment(sketch, "E492", {"start": v(-111.12, 3.37) * mm, "end": v(-111.12, 3.62) * mm});
            skLineSegment(sketch, "E493", {"start": v(-111.12, 3.62) * mm, "end": v(-111.12, 3.81) * mm});
            skLineSegment(sketch, "E494", {"start": v(-111.12, 3.81) * mm, "end": v(-110.9, 4.38) * mm});
            skLineSegment(sketch, "E495", {"start": v(-110.9, 4.38) * mm, "end": v(-110.22, 5) * mm});
            skLineSegment(sketch, "E496", {"start": v(-110.22, 5) * mm, "end": v(-108.96, 5.44) * mm});
            skLineSegment(sketch, "E497", {"start": v(-108.96, 5.44) * mm, "end": v(-107.52, 5.6) * mm});
            skLineSegment(sketch, "E498", {"start": v(-107.52, 5.6) * mm, "end": v(-107.04, 5.6) * mm});
            skLineSegment(sketch, "E499", {"start": v(-107.04, 5.6) * mm, "end": v(-106.61, 5.6) * mm});
            skLineSegment(sketch, "E500", {"start": v(-106.61, 5.6) * mm, "end": v(-105.32, 5.5) * mm});
            skLineSegment(sketch, "E501", {"start": v(-105.32, 5.5) * mm, "end": v(-103.69, 5.14) * mm});
            skLineSegment(sketch, "E502", {"start": v(-103.69, 5.14) * mm, "end": v(-102.34, 4.49) * mm});
            skLineSegment(sketch, "E503", {"start": v(-102.34, 4.49) * mm, "end": v(-101.62, 3.77) * mm});
            skLineSegment(sketch, "E504", {"start": v(-101.62, 3.77) * mm, "end": v(-101.5, 3.48) * mm});
            skLineSegment(sketch, "E505", {"start": v(-101.5, 3.48) * mm, "end": v(-98.3, 4.83) * mm});
            skLineSegment(sketch, "E506", {"start": v(-98.3, 4.83) * mm, "end": v(-98.52, 5.28) * mm});
            skLineSegment(sketch, "E507", {"start": v(-98.52, 5.28) * mm, "end": v(-99.63, 6.43) * mm});
            skLineSegment(sketch, "E508", {"start": v(-99.63, 6.43) * mm, "end": v(-101.7, 7.56) * mm});
            skLineSegment(sketch, "E509", {"start": v(-101.7, 7.56) * mm, "end": v(-104.3, 8.24) * mm});
            skLineSegment(sketch, "E510", {"start": v(-104.3, 8.24) * mm, "end": v(-106.54, 8.46) * mm});
            skLineSegment(sketch, "E511", {"start": v(-106.54, 8.46) * mm, "end": v(-107.28, 8.46) * mm});
            skLineSegment(sketch, "E512", {"start": v(-107.28, 8.46) * mm, "end": v(-107.96, 8.46) * mm});
            skLineSegment(sketch, "E513", {"start": v(-107.96, 8.46) * mm, "end": v(-109.99, 8.19) * mm});
            skLineSegment(sketch, "E514", {"start": v(-109.99, 8.19) * mm, "end": v(-112.4, 7.31) * mm});
            skLineSegment(sketch, "E515", {"start": v(-112.4, 7.31) * mm, "end": v(-114.14, 5.75) * mm});
            skLineSegment(sketch, "E516", {"start": v(-114.14, 5.75) * mm, "end": v(-114.8, 4) * mm});
            skLineSegment(sketch, "E517", {"start": v(-114.8, 4) * mm, "end": v(-114.8, 3.41) * mm});
            skLineSegment(sketch, "E518", {"start": v(-114.8, 3.41) * mm, "end": v(-114.8, 2.9) * mm});
            skLineSegment(sketch, "E519", {"start": v(-114.8, 2.9) * mm, "end": v(-114.28, 1.4) * mm});
            skLineSegment(sketch, "E520", {"start": v(-114.28, 1.4) * mm, "end": v(-112.76, 0.02) * mm});
            skLineSegment(sketch, "E521", {"start": v(-112.76, 0.02) * mm, "end": v(-110.35, -0.93) * mm});
            skLineSegment(sketch, "E522", {"start": v(-110.35, -0.93) * mm, "end": v(-107.94, -1.5) * mm});
            skLineSegment(sketch, "E523", {"start": v(-107.94, -1.5) * mm, "end": v(-107.13, -1.66) * mm});
            skLineSegment(sketch, "E524", {"start": v(-107.13, -1.66) * mm, "end": v(-106.56, -1.77) * mm});
            skLineSegment(sketch, "E525", {"start": v(-106.56, -1.77) * mm, "end": v(-104.83, -2.08) * mm});
            skLineSegment(sketch, "E526", {"start": v(-104.83, -2.08) * mm, "end": v(-102.87, -2.55) * mm});
            skLineSegment(sketch, "E527", {"start": v(-102.87, -2.55) * mm, "end": v(-101.51, -3.23) * mm});
            skLineSegment(sketch, "E528", {"start": v(-101.51, -3.23) * mm, "end": v(-101, -4.02) * mm});
            skLineSegment(sketch, "E529", {"start": v(-101, -4.02) * mm, "end": v(-101, -4.28) * mm});
            skLineSegment(sketch, "E530", {"start": v(-101, -4.28) * mm, "end": v(-101, -4.5) * mm});
            skLineSegment(sketch, "E531", {"start": v(-101, -4.5) * mm, "end": v(-101.29, -5.13) * mm});
            skLineSegment(sketch, "E532", {"start": v(-101.29, -5.13) * mm, "end": v(-102.18, -5.93) * mm});
            skLineSegment(sketch, "E533", {"start": v(-102.18, -5.93) * mm, "end": v(-103.75, -6.52) * mm});
            skLineSegment(sketch, "E534", {"start": v(-103.75, -6.52) * mm, "end": v(-105.49, -6.76) * mm});
            skLineSegment(sketch, "E535", {"start": v(-105.49, -6.76) * mm, "end": v(-106.07, -6.76) * mm});
            skLineSegment(sketch, "E536", {"start": v(-106.07, -6.76) * mm, "end": v(-106.54, -6.76) * mm});
            skLineSegment(sketch, "E537", {"start": v(-106.54, -6.76) * mm, "end": v(-107.97, -6.65) * mm});
            skLineSegment(sketch, "E538", {"start": v(-107.97, -6.65) * mm, "end": v(-109.71, -6.26) * mm});
            skLineSegment(sketch, "E539", {"start": v(-109.71, -6.26) * mm, "end": v(-111.12, -5.53) * mm});
            skLineSegment(sketch, "E540", {"start": v(-111.12, -5.53) * mm, "end": v(-111.89, -4.71) * mm});
            skLineSegment(sketch, "E541", {"start": v(-111.89, -4.71) * mm, "end": v(-112.03, -4.39) * mm});
            skLineSegment(sketch, "E542", {"start": v(-112.03, -4.39) * mm, "end": v(-115.12, -5.69) * mm});
            skLineSegment(sketch, "E543", {"start": v(-115.12, -5.69) * mm, "end": v(-114.9, -6.2) * mm});
            skLineSegment(sketch, "E544", {"start": v(-114.9, -6.2) * mm, "end": v(-113.8, -7.55) * mm});
            skLineSegment(sketch, "E545", {"start": v(-113.8, -7.55) * mm, "end": v(-111.84, -8.9) * mm});
            skLineSegment(sketch, "E546", {"start": v(-111.84, -8.9) * mm, "end": v(-109.39, -9.7) * mm});
            skLineSegment(sketch, "E547", {"start": v(-109.39, -9.7) * mm, "end": v(-107.29, -9.98) * mm});
            skLineSegment(sketch, "E548", {"start": v(-107.29, -9.98) * mm, "end": v(-106.58, -9.98) * mm});
            skLineSegment(sketch, "E549", {"start": v(-106.58, -9.98) * mm, "end": v(-105.92, -9.98) * mm});
            skLineSegment(sketch, "E550", {"start": v(-105.92, -9.98) * mm, "end": v(-103.95, -9.81) * mm});
            skLineSegment(sketch, "E551", {"start": v(-103.95, -9.81) * mm, "end": v(-101.85, -9.36) * mm});
            skLineSegment(sketch, "E552", {"start": v(-101.85, -9.36) * mm, "end": v(-100.22, -8.7) * mm});
            skLineSegment(sketch, "E553", {"start": v(-100.22, -8.7) * mm, "end": v(-99.02, -7.86) * mm});
            skLineSegment(sketch, "E554", {"start": v(-99.02, -7.86) * mm, "end": v(-98.17, -6.93) * mm});
            skLineSegment(sketch, "E555", {"start": v(-98.17, -6.93) * mm, "end": v(-97.65, -5.96) * mm});
            skLineSegment(sketch, "E556", {"start": v(-97.65, -5.96) * mm, "end": v(-97.37, -5.02) * mm});
            skLineSegment(sketch, "E557", {"start": v(-97.37, -5.02) * mm, "end": v(-97.29, -4.38) * mm});
            skLineSegment(sketch, "E558", {"start": v(-97.29, -4.38) * mm, "end": v(-97.29, -4.17) * mm});
            skLineSegment(sketch, "E559", {"start": v(-97.29, -4.17) * mm, "end": v(-97.29, -3.62) * mm});
            skLineSegment(sketch, "E560", {"start": v(-97.29, -3.62) * mm, "end": v(-97.89, -1.98) * mm});
            skLineSegment(sketch, "E561", {"start": v(-97.89, -1.98) * mm, "end": v(-99.47, -0.52) * mm});
            skLineSegment(sketch, "E562", {"start": v(-99.47, -0.52) * mm, "end": v(-101.7, 0.39) * mm});
            skLineSegment(sketch, "E563", {"start": v(-101.7, 0.39) * mm, "end": v(-103.6, 0.85) * mm});
            skLineSegment(sketch, "E564", {"start": v(-103.6, 0.85) * mm, "end": v(-104.25, 0.96) * mm});
            skLineSegment(sketch, "E565", {"start": v(-85.87, -6.75) * mm, "end": v(-86.42, -6.75) * mm});
            skLineSegment(sketch, "E566", {"start": v(-86.42, -6.75) * mm, "end": v(-88.08, -6.48) * mm});
            skLineSegment(sketch, "E567", {"start": v(-88.08, -6.48) * mm, "end": v(-90.2, -5.53) * mm});
            skLineSegment(sketch, "E568", {"start": v(-90.2, -5.53) * mm, "end": v(-91.8, -3.65) * mm});
            skLineSegment(sketch, "E569", {"start": v(-91.8, -3.65) * mm, "end": v(-92.42, -1.38) * mm});
            skLineSegment(sketch, "E570", {"start": v(-92.42, -1.38) * mm, "end": v(-92.42, -0.63) * mm});
            skLineSegment(sketch, "E571", {"start": v(-92.42, -0.63) * mm, "end": v(-92.42, -0.2) * mm});
            skLineSegment(sketch, "E572", {"start": v(-92.42, -0.2) * mm, "end": v(-92.23, 1.06) * mm});
            skLineSegment(sketch, "E573", {"start": v(-92.23, 1.06) * mm, "end": v(-91.73, 2.4) * mm});
            skLineSegment(sketch, "E574", {"start": v(-91.73, 2.4) * mm, "end": v(-90.98, 3.46) * mm});
            skLineSegment(sketch, "E575", {"start": v(-90.98, 3.46) * mm, "end": v(-90.05, 4.23) * mm});
            skLineSegment(sketch, "E576", {"start": v(-90.05, 4.23) * mm, "end": v(-89, 4.78) * mm});
            skLineSegment(sketch, "E577", {"start": v(-89, 4.78) * mm, "end": v(-87.91, 5.13) * mm});
            skLineSegment(sketch, "E578", {"start": v(-87.91, 5.13) * mm, "end": v(-86.84, 5.3) * mm});
            skLineSegment(sketch, "E579", {"start": v(-86.84, 5.3) * mm, "end": v(-86.11, 5.36) * mm});
            skLineSegment(sketch, "E580", {"start": v(-86.11, 5.36) * mm, "end": v(-85.87, 5.36) * mm});
            skLineSegment(sketch, "E581", {"start": v(-85.87, 5.36) * mm, "end": v(-85.62, 5.36) * mm});
            skLineSegment(sketch, "E582", {"start": v(-85.62, 5.36) * mm, "end": v(-84.9, 5.3) * mm});
            skLineSegment(sketch, "E583", {"start": v(-84.9, 5.3) * mm, "end": v(-83.82, 5.13) * mm});
            skLineSegment(sketch, "E584", {"start": v(-83.82, 5.13) * mm, "end": v(-82.73, 4.78) * mm});
            skLineSegment(sketch, "E585", {"start": v(-82.73, 4.78) * mm, "end": v(-81.68, 4.23) * mm});
            skLineSegment(sketch, "E586", {"start": v(-81.68, 4.23) * mm, "end": v(-80.75, 3.46) * mm});
            skLineSegment(sketch, "E587", {"start": v(-80.75, 3.46) * mm, "end": v(-80, 2.4) * mm});
            skLineSegment(sketch, "E588", {"start": v(-80, 2.4) * mm, "end": v(-79.5, 1.06) * mm});
            skLineSegment(sketch, "E589", {"start": v(-79.5, 1.06) * mm, "end": v(-79.32, -0.2) * mm});
            skLineSegment(sketch, "E590", {"start": v(-79.32, -0.2) * mm, "end": v(-79.32, -0.63) * mm});
            skLineSegment(sketch, "E591", {"start": v(-79.32, -0.63) * mm, "end": v(-79.32, -1.38) * mm});
            skLineSegment(sketch, "E592", {"start": v(-79.32, -1.38) * mm, "end": v(-79.94, -3.65) * mm});
            skLineSegment(sketch, "E593", {"start": v(-79.94, -3.65) * mm, "end": v(-81.53, -5.53) * mm});
            skLineSegment(sketch, "E594", {"start": v(-81.53, -5.53) * mm, "end": v(-83.65, -6.48) * mm});
            skLineSegment(sketch, "E595", {"start": v(-83.65, -6.48) * mm, "end": v(-85.31, -6.75) * mm});
            skLineSegment(sketch, "E596", {"start": v(-85.31, -6.75) * mm, "end": v(-85.87, -6.75) * mm});
            skLineSegment(sketch, "E597", {"start": v(-85.87, 8.47) * mm, "end": v(-86.3, 8.47) * mm});
            skLineSegment(sketch, "E598", {"start": v(-86.3, 8.47) * mm, "end": v(-87.62, 8.36) * mm});
            skLineSegment(sketch, "E599", {"start": v(-87.62, 8.36) * mm, "end": v(-89.38, 8) * mm});
            skLineSegment(sketch, "E600", {"start": v(-89.38, 8) * mm, "end": v(-91.07, 7.39) * mm});
            skLineSegment(sketch, "E601", {"start": v(-91.07, 7.39) * mm, "end": v(-92.62, 6.48) * mm});
            skLineSegment(sketch, "E602", {"start": v(-92.62, 6.48) * mm, "end": v(-93.95, 5.25) * mm});
            skLineSegment(sketch, "E603", {"start": v(-93.95, 5.25) * mm, "end": v(-95, 3.68) * mm});
            skLineSegment(sketch, "E604", {"start": v(-95, 3.68) * mm, "end": v(-95.67, 1.74) * mm});
            skLineSegment(sketch, "E605", {"start": v(-95.67, 1.74) * mm, "end": v(-95.91, 0) * mm});
            skLineSegment(sketch, "E606", {"start": v(-95.91, 0) * mm, "end": v(-95.91, -0.6) * mm});
            skLineSegment(sketch, "E607", {"start": v(-95.91, -0.6) * mm, "end": v(-95.91, -1.17) * mm});
            skLineSegment(sketch, "E608", {"start": v(-95.91, -1.17) * mm, "end": v(-95.7, -2.91) * mm});
            skLineSegment(sketch, "E609", {"start": v(-95.7, -2.91) * mm, "end": v(-95.07, -4.87) * mm});
            skLineSegment(sketch, "E610", {"start": v(-95.07, -4.87) * mm, "end": v(-94.1, -6.48) * mm});
            skLineSegment(sketch, "E611", {"start": v(-94.1, -6.48) * mm, "end": v(-92.82, -7.75) * mm});
            skLineSegment(sketch, "E612", {"start": v(-92.82, -7.75) * mm, "end": v(-91.3, -8.72) * mm});
            skLineSegment(sketch, "E613", {"start": v(-91.3, -8.72) * mm, "end": v(-89.6, -9.38) * mm});
            skLineSegment(sketch, "E614", {"start": v(-89.6, -9.38) * mm, "end": v(-87.78, -9.77) * mm});
            skLineSegment(sketch, "E615", {"start": v(-87.78, -9.77) * mm, "end": v(-86.34, -9.9) * mm});
            skLineSegment(sketch, "E616", {"start": v(-86.34, -9.9) * mm, "end": v(-85.87, -9.9) * mm});
            skLineSegment(sketch, "E617", {"start": v(-85.87, -9.9) * mm, "end": v(-85.39, -9.9) * mm});
            skLineSegment(sketch, "E618", {"start": v(-85.39, -9.9) * mm, "end": v(-83.96, -9.77) * mm});
            skLineSegment(sketch, "E619", {"start": v(-83.96, -9.77) * mm, "end": v(-82.13, -9.38) * mm});
            skLineSegment(sketch, "E620", {"start": v(-82.13, -9.38) * mm, "end": v(-80.43, -8.72) * mm});
            skLineSegment(sketch, "E621", {"start": v(-80.43, -8.72) * mm, "end": v(-78.92, -7.75) * mm});
            skLineSegment(sketch, "E622", {"start": v(-78.92, -7.75) * mm, "end": v(-77.64, -6.48) * mm});
            skLineSegment(sketch, "E623", {"start": v(-77.64, -6.48) * mm, "end": v(-76.67, -4.87) * mm});
            skLineSegment(sketch, "E624", {"start": v(-76.67, -4.87) * mm, "end": v(-76.04, -2.91) * mm});
            skLineSegment(sketch, "E625", {"start": v(-76.04, -2.91) * mm, "end": v(-75.82, -1.17) * mm});
            skLineSegment(sketch, "E626", {"start": v(-75.82, -1.17) * mm, "end": v(-75.82, -0.6) * mm});
            skLineSegment(sketch, "E627", {"start": v(-75.82, -0.6) * mm, "end": v(-75.82, 0) * mm});
            skLineSegment(sketch, "E628", {"start": v(-75.82, 0) * mm, "end": v(-76.07, 1.74) * mm});
            skLineSegment(sketch, "E629", {"start": v(-76.07, 1.74) * mm, "end": v(-76.74, 3.68) * mm});
            skLineSegment(sketch, "E630", {"start": v(-76.74, 3.68) * mm, "end": v(-77.79, 5.25) * mm});
            skLineSegment(sketch, "E631", {"start": v(-77.79, 5.25) * mm, "end": v(-79.12, 6.48) * mm});
            skLineSegment(sketch, "E632", {"start": v(-79.12, 6.48) * mm, "end": v(-80.67, 7.39) * mm});
            skLineSegment(sketch, "E633", {"start": v(-80.67, 7.39) * mm, "end": v(-82.36, 8) * mm});
            skLineSegment(sketch, "E634", {"start": v(-82.36, 8) * mm, "end": v(-84.11, 8.36) * mm});
            skLineSegment(sketch, "E635", {"start": v(-84.11, 8.36) * mm, "end": v(-85.43, 8.47) * mm});
            skLineSegment(sketch, "E636", {"start": v(-85.43, 8.47) * mm, "end": v(-85.87, 8.47) * mm});
            skLineSegment(sketch, "E637", {"start": v(9.39, -9.63) * mm, "end": v(9.15, -9.77) * mm});
            skLineSegment(sketch, "E638", {"start": v(9.15, -9.77) * mm, "end": v(8.44, -10.13) * mm});
            skLineSegment(sketch, "E639", {"start": v(8.44, -10.13) * mm, "end": v(7.27, -10.66) * mm});
            skLineSegment(sketch, "E640", {"start": v(7.27, -10.66) * mm, "end": v(5.66, -11.25) * mm});
            skLineSegment(sketch, "E641", {"start": v(5.66, -11.25) * mm, "end": v(3.62, -11.85) * mm});
            skLineSegment(sketch, "E642", {"start": v(3.62, -11.85) * mm, "end": v(1.17, -12.37) * mm});
            skLineSegment(sketch, "E643", {"start": v(1.17, -12.37) * mm, "end": v(-1.68, -12.74) * mm});
            skLineSegment(sketch, "E644", {"start": v(-1.68, -12.74) * mm, "end": v(-4.1, -12.88) * mm});
            skLineSegment(sketch, "E645", {"start": v(-4.1, -12.88) * mm, "end": v(-4.92, -12.88) * mm});
            skLineSegment(sketch, "E646", {"start": v(-4.92, -12.88) * mm, "end": v(-5.55, -12.88) * mm});
            skLineSegment(sketch, "E647", {"start": v(-5.55, -12.88) * mm, "end": v(-7.45, -12.78) * mm});
            skLineSegment(sketch, "E648", {"start": v(-7.45, -12.78) * mm, "end": v(-9.66, -12.45) * mm});
            skLineSegment(sketch, "E649", {"start": v(-9.66, -12.45) * mm, "end": v(-11.45, -11.9) * mm});
            skLineSegment(sketch, "E650", {"start": v(-11.45, -11.9) * mm, "end": v(-12.44, -11.35) * mm});
            skLineSegment(sketch, "E651", {"start": v(-12.44, -11.35) * mm, "end": v(-12.7, -11.1) * mm});
            skLineSegment(sketch, "E652", {"start": v(-12.7, -11.1) * mm, "end": v(-12.95, -10.85) * mm});
            skLineSegment(sketch, "E653", {"start": v(-12.95, -10.85) * mm, "end": v(-13.58, -9.97) * mm});
            skLineSegment(sketch, "E654", {"start": v(-13.58, -9.97) * mm, "end": v(-14.22, -8.6) * mm});
            skLineSegment(sketch, "E655", {"start": v(-14.22, -8.6) * mm, "end": v(-14.6, -7.1) * mm});
            skLineSegment(sketch, "E656", {"start": v(-14.6, -7.1) * mm, "end": v(-14.74, -5.96) * mm});
            skLineSegment(sketch, "E657", {"start": v(-14.74, -5.96) * mm, "end": v(-14.74, -5.57) * mm});
            skLineSegment(sketch, "E658", {"start": v(-14.74, -5.57) * mm, "end": v(-14.74, -5.27) * mm});
            skLineSegment(sketch, "E659", {"start": v(-14.74, -5.27) * mm, "end": v(-14.6, -4.34) * mm});
            skLineSegment(sketch, "E660", {"start": v(-14.6, -4.34) * mm, "end": v(-14.2, -3.33) * mm});
            skLineSegment(sketch, "E661", {"start": v(-14.2, -3.33) * mm, "end": v(-13.5, -2.64) * mm});
            skLineSegment(sketch, "E662", {"start": v(-13.5, -2.64) * mm, "end": v(-12.77, -2.39) * mm});
            skLineSegment(sketch, "E663", {"start": v(-12.77, -2.39) * mm, "end": v(-12.52, -2.39) * mm});
            skLineSegment(sketch, "E664", {"start": v(-12.52, -2.39) * mm, "end": v(-12.07, -2.39) * mm});
            skLineSegment(sketch, "E665", {"start": v(-12.07, -2.39) * mm, "end": v(-10.72, -2.65) * mm});
            skLineSegment(sketch, "E666", {"start": v(-10.72, -2.65) * mm, "end": v(-8.33, -3.36) * mm});
            skLineSegment(sketch, "E667", {"start": v(-8.33, -3.36) * mm, "end": v(-5.5, -4.38) * mm});
            skLineSegment(sketch, "E668", {"start": v(-5.5, -4.38) * mm, "end": v(-2.4, -5.58) * mm});
            skLineSegment(sketch, "E669", {"start": v(-2.4, -5.58) * mm, "end": v(0.8, -6.83) * mm});
            skLineSegment(sketch, "E670", {"start": v(0.8, -6.83) * mm, "end": v(3.95, -8.01) * mm});
            skLineSegment(sketch, "E671", {"start": v(3.95, -8.01) * mm, "end": v(6.86, -8.99) * mm});
            skLineSegment(sketch, "E672", {"start": v(6.86, -8.99) * mm, "end": v(8.75, -9.5) * mm});
            skLineSegment(sketch, "E673", {"start": v(8.75, -9.5) * mm, "end": v(9.39, -9.63) * mm});
            skLineSegment(sketch, "E674", {"start": v(-7.86, 9.23) * mm, "end": v(-7.81, 9.26) * mm});
            skLineSegment(sketch, "E675", {"start": v(-7.81, 9.26) * mm, "end": v(-7.28, 9.6) * mm});
            skLineSegment(sketch, "E676", {"start": v(-7.28, 9.6) * mm, "end": v(-7.23, 9.62) * mm});
            skLineSegment(sketch, "E677", {"start": v(-7.23, 9.62) * mm, "end": v(-7.16, 9.66) * mm});
            skLineSegment(sketch, "E678", {"start": v(-7.16, 9.66) * mm, "end": v(-7.23, 9.67) * mm});
            skLineSegment(sketch, "E679", {"start": v(-7.23, 9.67) * mm, "end": v(-7.97, 9.87) * mm});
            skLineSegment(sketch, "E680", {"start": v(-7.97, 9.87) * mm, "end": v(-10.25, 10.27) * mm});
            skLineSegment(sketch, "E681", {"start": v(-10.25, 10.27) * mm, "end": v(-12.96, 10.31) * mm});
            skLineSegment(sketch, "E682", {"start": v(-12.96, 10.31) * mm, "end": v(-15.04, 9.66) * mm});
            skLineSegment(sketch, "E683", {"start": v(-15.04, 9.66) * mm, "end": v(-16.06, 8.6) * mm});
            skLineSegment(sketch, "E684", {"start": v(-16.06, 8.6) * mm, "end": v(-16.19, 8.19) * mm});
            skLineSegment(sketch, "E685", {"start": v(-16.19, 8.19) * mm, "end": v(-16.28, 7.9) * mm});
            skLineSegment(sketch, "E686", {"start": v(-16.28, 7.9) * mm, "end": v(-16.24, 6.94) * mm});
            skLineSegment(sketch, "E687", {"start": v(-16.24, 6.94) * mm, "end": v(-15.7, 5.7) * mm});
            skLineSegment(sketch, "E688", {"start": v(-15.7, 5.7) * mm, "end": v(-14.72, 4.47) * mm});
            skLineSegment(sketch, "E689", {"start": v(-14.72, 4.47) * mm, "end": v(-13.42, 3.3) * mm});
            skLineSegment(sketch, "E690", {"start": v(-13.42, 3.3) * mm, "end": v(-11.92, 2.21) * mm});
            skLineSegment(sketch, "E691", {"start": v(-11.92, 2.21) * mm, "end": v(-10.36, 1.22) * mm});
            skLineSegment(sketch, "E692", {"start": v(-10.36, 1.22) * mm, "end": v(-8.87, 0.35) * mm});
            skLineSegment(sketch, "E693", {"start": v(-8.87, 0.35) * mm, "end": v(-7.9, -0.19) * mm});
            skLineSegment(sketch, "E694", {"start": v(-7.9, -0.19) * mm, "end": v(-7.57, -0.37) * mm});
            skLineSegment(sketch, "E695", {"start": v(-7.57, -0.37) * mm, "end": v(-7.48, -0.42) * mm});
            skLineSegment(sketch, "E696", {"start": v(-7.48, -0.42) * mm, "end": v(-7.15, -0.53) * mm});
            skLineSegment(sketch, "E697", {"start": v(-7.15, -0.53) * mm, "end": v(-6.9, -0.5) * mm});
            skLineSegment(sketch, "E698", {"start": v(-6.9, -0.5) * mm, "end": v(-6.86, -0.33) * mm});
            skLineSegment(sketch, "E699", {"start": v(-6.86, -0.33) * mm, "end": v(-6.99, -0.08) * mm});
            skLineSegment(sketch, "E700", {"start": v(-6.99, -0.08) * mm, "end": v(-7.05, -0.02) * mm});
            skLineSegment(sketch, "E701", {"start": v(-7.05, -0.02) * mm, "end": v(-7.24, 0.21) * mm});
            skLineSegment(sketch, "E702", {"start": v(-7.24, 0.21) * mm, "end": v(-7.8, 0.92) * mm});
            skLineSegment(sketch, "E703", {"start": v(-7.8, 0.92) * mm, "end": v(-8.55, 2.01) * mm});
            skLineSegment(sketch, "E704", {"start": v(-8.55, 2.01) * mm, "end": v(-9.2, 3.21) * mm});
            skLineSegment(sketch, "E705", {"start": v(-9.2, 3.21) * mm, "end": v(-9.65, 4.48) * mm});
            skLineSegment(sketch, "E706", {"start": v(-9.65, 4.48) * mm, "end": v(-9.84, 5.76) * mm});
            skLineSegment(sketch, "E707", {"start": v(-9.84, 5.76) * mm, "end": v(-9.66, 7) * mm});
            skLineSegment(sketch, "E708", {"start": v(-9.66, 7) * mm, "end": v(-9.03, 8.18) * mm});
            skLineSegment(sketch, "E709", {"start": v(-9.03, 8.18) * mm, "end": v(-8.18, 9.02) * mm});
            skLineSegment(sketch, "E710", {"start": v(-8.18, 9.02) * mm, "end": v(-7.86, 9.23) * mm});
            skLineSegment(sketch, "E711", {"start": v(-7.17, 9.66) * mm, "end": v(-6.93, 9.8) * mm});
            skLineSegment(sketch, "E712", {"start": v(-6.93, 9.8) * mm, "end": v(-6.22, 10.17) * mm});
            skLineSegment(sketch, "E713", {"start": v(-6.22, 10.17) * mm, "end": v(-5.05, 10.69) * mm});
            skLineSegment(sketch, "E714", {"start": v(-5.05, 10.69) * mm, "end": v(-3.44, 11.28) * mm});
            skLineSegment(sketch, "E715", {"start": v(-3.44, 11.28) * mm, "end": v(-1.4, 11.88) * mm});
            skLineSegment(sketch, "E716", {"start": v(-1.4, 11.88) * mm, "end": v(1.05, 12.4) * mm});
            skLineSegment(sketch, "E717", {"start": v(1.05, 12.4) * mm, "end": v(3.9, 12.77) * mm});
            skLineSegment(sketch, "E718", {"start": v(3.9, 12.77) * mm, "end": v(6.33, 12.91) * mm});
            skLineSegment(sketch, "E719", {"start": v(6.33, 12.91) * mm, "end": v(7.14, 12.91) * mm});
            skLineSegment(sketch, "E720", {"start": v(7.14, 12.91) * mm, "end": v(7.77, 12.91) * mm});
            skLineSegment(sketch, "E721", {"start": v(7.77, 12.91) * mm, "end": v(9.67, 12.8) * mm});
            skLineSegment(sketch, "E722", {"start": v(9.67, 12.8) * mm, "end": v(11.88, 12.49) * mm});
            skLineSegment(sketch, "E723", {"start": v(11.88, 12.49) * mm, "end": v(13.67, 11.93) * mm});
            skLineSegment(sketch, "E724", {"start": v(13.67, 11.93) * mm, "end": v(14.66, 11.38) * mm});
            skLineSegment(sketch, "E725", {"start": v(14.66, 11.38) * mm, "end": v(14.92, 11.13) * mm});
            skLineSegment(sketch, "E726", {"start": v(14.92, 11.13) * mm, "end": v(15.17, 10.88) * mm});
            skLineSegment(sketch, "E727", {"start": v(15.17, 10.88) * mm, "end": v(15.8, 10) * mm});
            skLineSegment(sketch, "E728", {"start": v(15.8, 10) * mm, "end": v(16.44, 8.64) * mm});
            skLineSegment(sketch, "E729", {"start": v(16.44, 8.64) * mm, "end": v(16.83, 7.14) * mm});
            skLineSegment(sketch, "E730", {"start": v(16.83, 7.14) * mm, "end": v(16.96, 5.99) * mm});
            skLineSegment(sketch, "E731", {"start": v(16.96, 5.99) * mm, "end": v(16.96, 5.6) * mm});
            skLineSegment(sketch, "E732", {"start": v(16.96, 5.6) * mm, "end": v(16.96, 5.3) * mm});
            skLineSegment(sketch, "E733", {"start": v(16.96, 5.3) * mm, "end": v(16.83, 4.38) * mm});
            skLineSegment(sketch, "E734", {"start": v(16.83, 4.38) * mm, "end": v(16.42, 3.36) * mm});
            skLineSegment(sketch, "E735", {"start": v(16.42, 3.36) * mm, "end": v(15.72, 2.67) * mm});
            skLineSegment(sketch, "E736", {"start": v(15.72, 2.67) * mm, "end": v(14.99, 2.42) * mm});
            skLineSegment(sketch, "E737", {"start": v(14.99, 2.42) * mm, "end": v(14.74, 2.42) * mm});
            skLineSegment(sketch, "E738", {"start": v(14.74, 2.42) * mm, "end": v(14.3, 2.42) * mm});
            skLineSegment(sketch, "E739", {"start": v(14.3, 2.42) * mm, "end": v(12.95, 2.68) * mm});
            skLineSegment(sketch, "E740", {"start": v(12.95, 2.68) * mm, "end": v(10.55, 3.39) * mm});
            skLineSegment(sketch, "E741", {"start": v(10.55, 3.39) * mm, "end": v(7.72, 4.4) * mm});
            skLineSegment(sketch, "E742", {"start": v(7.72, 4.4) * mm, "end": v(4.62, 5.6) * mm});
            skLineSegment(sketch, "E743", {"start": v(4.62, 5.6) * mm, "end": v(1.41, 6.87) * mm});
            skLineSegment(sketch, "E744", {"start": v(1.41, 6.87) * mm, "end": v(-1.73, 8.05) * mm});
            skLineSegment(sketch, "E745", {"start": v(-1.73, 8.05) * mm, "end": v(-4.64, 9.02) * mm});
            skLineSegment(sketch, "E746", {"start": v(-4.64, 9.02) * mm, "end": v(-6.53, 9.54) * mm});
            skLineSegment(sketch, "E747", {"start": v(-6.53, 9.54) * mm, "end": v(-7.17, 9.66) * mm});
            skSolve(sketch);
        }
        {
            var Q0;
            {var subQ5=sQuery(id+"F0.wireOp",EDGE,"E712");Q0=makeQuery(id+"F0.imprint","IMPRINT",FACE,{"disambiguationData":[TD([[makeQuery(id+"F0.imprint","IMPRINT",EDGE,{"derivedFrom":subQ5}),-1.0]])]});}
            var Q1;
            Q1=makeQuery(id+"F0.imprint","IMPRINT",FACE,{"disambiguationData":[TD([[makeQuery(id+"F0.imprint","IMPRINT",EDGE,{"derivedFrom":sQuery(id+"F0.wireOp",EDGE,"E37")}),-1.0]])]});
            var Q2;
            Q2=makeQuery(id+"F0.imprint","IMPRINT",FACE,{"disambiguationData":[TD([[makeQuery(id+"F0.imprint","IMPRINT",EDGE,{"derivedFrom":sQuery(id+"F0.wireOp",EDGE,"E74")}),-1.0]])]});
            var Q3;
            Q3=makeQuery(id+"F0.imprint","IMPRINT",FACE,{"disambiguationData":[TD([[makeQuery(id+"F0.imprint","IMPRINT",EDGE,{"derivedFrom":sQuery(id+"F0.wireOp",EDGE,"E169")}),1.0]])]});
            var Q4;
            Q4=makeQuery(id+"F0.imprint","IMPRINT",FACE,{"disambiguationData":[TD([[makeQuery(id+"F0.imprint","IMPRINT",EDGE,{"derivedFrom":sQuery(id+"F0.wireOp",EDGE,"E469")}),1.0]])]});
            var Q5;
            Q5=makeQuery(id+"F0.imprint","IMPRINT",FACE,{"disambiguationData":[TD([[makeQuery(id+"F0.imprint","IMPRINT",EDGE,{"derivedFrom":sQuery(id+"F0.wireOp",EDGE,"E187")}),-1.0]])]});
            var Q6;
            Q6=makeQuery(id+"F0.imprint","IMPRINT",FACE,{"disambiguationData":[TD([[makeQuery(id+"F0.imprint","IMPRINT",EDGE,{"derivedFrom":sQuery(id+"F0.wireOp",EDGE,"E335")}),-1.0]])]});
            var Q7;
            Q7=makeQuery(id+"F0.imprint","IMPRINT",FACE,{"disambiguationData":[TD([[makeQuery(id+"F0.imprint","IMPRINT",EDGE,{"derivedFrom":sQuery(id+"F0.wireOp",EDGE,"E402")}),-1.0]])]});
            var Q8;
            {var subQ0=sQuery(id+"F0.wireOp",EDGE,"E638");Q8=makeQuery(id+"F0.imprint","IMPRINT",FACE,{"disambiguationData":[TD([[makeQuery(id+"F0.imprint","IMPRINT",EDGE,{"derivedFrom":subQ0}),-1.0]])]});}
            var Q9;
            Q9=makeQuery(id+"F0.imprint","IMPRINT",FACE,{"disambiguationData":[TD([[makeQuery(id+"F0.imprint","IMPRINT",EDGE,{"derivedFrom":sQuery(id+"F0.wireOp",EDGE,"E78")}),-1.0]])]});
            var Q10;
            Q10=makeQuery(id+"F0.imprint","IMPRINT",FACE,{"disambiguationData":[TD([[makeQuery(id+"F0.imprint","IMPRINT",EDGE,{"derivedFrom":sQuery(id+"F0.wireOp",EDGE,"E674")}),1.0]])]});
            var Q11;
            Q11=makeQuery(id+"F0.imprint","IMPRINT",FACE,{"disambiguationData":[TD([[makeQuery(id+"F0.imprint","IMPRINT",EDGE,{"derivedFrom":sQuery(id+"F0.wireOp",EDGE,"E257")}),1.0]])]});
            var Q12;
            Q12=makeQuery(id+"F0.imprint","IMPRINT",FACE,{"disambiguationData":[TD([[makeQuery(id+"F0.imprint","IMPRINT",EDGE,{"derivedFrom":sQuery(id+"F0.wireOp",EDGE,"E0")}),1.0]])]});
            var Q13;
            Q13=makeQuery(id+"F0.imprint","IMPRINT",FACE,{"disambiguationData":[TD([[makeQuery(id+"F0.imprint","IMPRINT",EDGE,{"derivedFrom":sQuery(id+"F0.wireOp",EDGE,"E487")}),1.0]])]});
            var Q14;
            Q14=makeQuery(id+"F0.imprint","IMPRINT",FACE,{"disambiguationData":[TD([[makeQuery(id+"F0.imprint","IMPRINT",EDGE,{"derivedFrom":sQuery(id+"F0.wireOp",EDGE,"E145")}),1.0]])]});
            var Q15;
            {var subQ0=sQuery(id+"F0.wireOp",EDGE,"E4");var subQ1=sQuery(id+"F0.wireOp",EDGE,"E3");var subQ2=makeQuery(id+"F0.imprint","INTERSECT",VERTEX,{"derivedFrom":[subQ1,subQ0]});Q15=makeQuery(id+"F0.imprint","IMPRINT",FACE,{"disambiguationData":[TD([[makeQuery(id+"F0.imprint","IMPRINT",EDGE,{"disambiguationData":[TD([[subQ2,1.0]])],"derivedFrom":subQ1}),1.0]])]});}
            var Q16;
            {var subQ0=sQuery(id+"F0.wireOp",EDGE,"E678");var subQ1=sQuery(id+"F0.wireOp",EDGE,"E677");var subQ2=makeQuery(id+"F0.imprint","INTERSECT",VERTEX,{"derivedFrom":[subQ1,subQ0]});Q16=makeQuery(id+"F0.imprint","IMPRINT",FACE,{"disambiguationData":[TD([[makeQuery(id+"F0.imprint","IMPRINT",EDGE,{"disambiguationData":[TD([[subQ2,1.0]])],"derivedFrom":subQ1}),1.0]])]});}
            var Q17;
            Q17=makeQuery(id+"F0.imprint","IMPRINT",FACE,{"disambiguationData":[TD([[makeQuery(id+"F0.imprint","IMPRINT",EDGE,{"derivedFrom":sQuery(id+"F0.wireOp",EDGE,"E565")}),1.0]])]});
            extrude(context, id + "F1", {"entities" : qUnion([Q0, Q1, Q2, Q3, Q4, Q5, Q6, Q7, Q8, Q9, Q10, Q11, Q12, Q13, Q14, Q15, Q16, Q17]), "depth" : 12.7 * mm, "offsetDistance" : 25.4 * mm});
        }
        {
            var Q0;
            Q0=qCreatedBy(makeId("Top.planeOp"),FACE);
            var sketch = newSketch(context, id + "F2", { "sketchPlane" : qUnion([Q0])});
            skText(sketch, "E748", { "text": "DAK", "fontName": "OpenSans-Regular.ttf"});
            const initialGuessF2  = {"E748": [-0.08353, 0.0511, 1, 0, 0.05895]};
            skSetInitialGuess(sketch, initialGuessF2);
            skSolve(sketch);
        }
        {
            var Q0;
            Q0 = qSketchRegion(id + "F2", true);
            extrude(context, id + "F3", {"entities" : qUnion([Q0]), "depth" : 25.4 * mm, "offsetDistance" : 25.4 * mm});
        }
        {
            var Q0;
            Q0=qCreatedBy(makeId("Top.planeOp"),FACE);
            var sketch = newSketch(context, id + "F4", { "sketchPlane" : qUnion([Q0])});
            skLineSegment(sketch, "E749.bottom", {"start": v(-161.95, 134.95) * mm, "end": v(161.95, 134.95) * mm});
            skLineSegment(sketch, "E749.top", {"start": v(-161.95, -40.04) * mm, "end": v(161.95, -40.04) * mm});
            skLineSegment(sketch, "E749.left", {"start": v(-179.73, 117.17) * mm, "end": v(-179.73, -22.26) * mm});
            skLineSegment(sketch, "E749.right", {"start": v(179.73, 117.17) * mm, "end": v(179.73, -22.26) * mm});
            skPoint(sketch, "E750.visualSharp", {"position": v(-179.73, 134.95) * mm});
            skArc(sketch, "E750.filletArc", {"start": v(-161.95, 134.95) * mm, "mid": v(-174.53, 129.74) * mm, "end": v(-179.73, 117.17) * mm});
            skPoint(sketch, "E751.visualSharp", {"position": v(179.73, 134.95) * mm});
            skArc(sketch, "E751.filletArc", {"start": v(179.73, 117.17) * mm, "mid": v(174.53, 129.74) * mm, "end": v(161.95, 134.95) * mm});
            skPoint(sketch, "E752.visualSharp", {"position": v(179.73, -40.04) * mm});
            skArc(sketch, "E752.filletArc", {"start": v(161.95, -40.04) * mm, "mid": v(174.53, -34.83) * mm, "end": v(179.73, -22.26) * mm});
            skPoint(sketch, "E753.visualSharp", {"position": v(-179.73, -40.04) * mm});
            skArc(sketch, "E753.filletArc", {"start": v(-179.73, -22.26) * mm, "mid": v(-174.53, -34.83) * mm, "end": v(-161.95, -40.04) * mm});
            skSolve(sketch);
        }
        {
            var Q0;
            Q0=makeQuery(id+"F4.imprint","IMPRINT",FACE,{"disambiguationData":[TD([[makeQuery(id+"F4.imprint","IMPRINT",EDGE,{"derivedFrom":sQuery(id+"F4.wireOp",EDGE,"E749.bottom")}),-1.0]])]});
            extrude(context, id + "F5", {"entities" : qUnion([Q0]), "oppositeDirection" : true, "depth" : 5.08 * mm, "offsetDistance" : 25.4 * mm});
        }
    });
